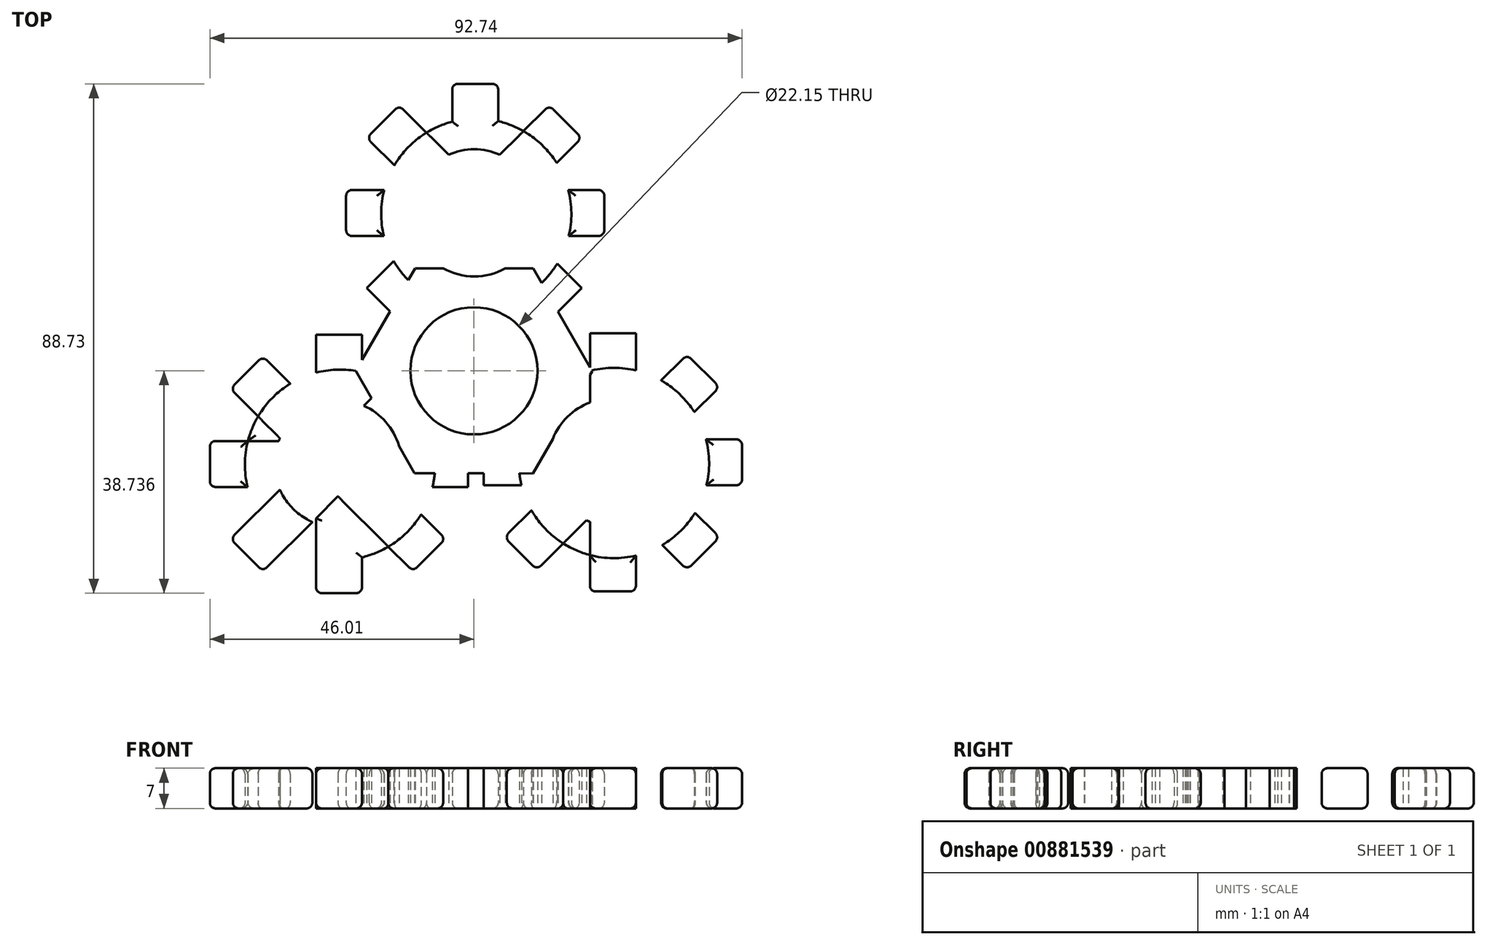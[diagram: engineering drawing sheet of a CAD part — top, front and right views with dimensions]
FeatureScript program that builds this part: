
annotation { "Feature Type Name" : "Feature", "Feature Type Description" : "" }
export const myFeature = defineFeature(function(context is Context, id is Id, definition is map)
    precondition{}
    {
        {
            var Q0;
            Q0=qCreatedBy(makeId("Top.planeOp"),FACE);
            var sketch = newSketch(context, id + "F0", { "sketchPlane" : qUnion([Q0])});
            skLineSegment(sketch, "E0.bottom", {"start": v(28.23, -45) * mm, "end": v(20.23, -45) * mm});
            skLineSegment(sketch, "E0.top", {"start": v(28.23, 0) * mm, "end": v(20.23, 0) * mm});
            skLineSegment(sketch, "E0.left", {"start": v(28.23, -45) * mm, "end": v(28.23, 0) * mm});
            skLineSegment(sketch, "E0.right", {"start": v(20.23, -45) * mm, "end": v(20.23, 0) * mm});
            skPoint(sketch, "E0.middle", {"position": v(24.23, -22.5) * mm});
            skLineSegment(sketch, "E1.bottom", {"start": v(46.73, -26.5) * mm, "end": v(1.73, -26.5) * mm});
            skLineSegment(sketch, "E1.top", {"start": v(46.73, -18.5) * mm, "end": v(1.73, -18.5) * mm});
            skLineSegment(sketch, "E1.left", {"start": v(46.73, -26.5) * mm, "end": v(46.73, -18.5) * mm});
            skLineSegment(sketch, "E1.right", {"start": v(1.73, -26.5) * mm, "end": v(1.73, -18.5) * mm});
            skPoint(sketch, "E2.middle", {"position": v(24.41, -22.64) * mm});
            skLineSegment(sketch, "E3.bottom", {"start": v(42.8, -35.57) * mm, "end": v(37.14, -41.22) * mm});
            skLineSegment(sketch, "E3.top", {"start": v(10.98, -3.75) * mm, "end": v(5.32, -9.4) * mm});
            skLineSegment(sketch, "E3.left", {"start": v(42.8, -35.57) * mm, "end": v(10.98, -3.75) * mm});
            skLineSegment(sketch, "E3.right", {"start": v(37.14, -41.22) * mm, "end": v(5.32, -9.4) * mm});
            skPoint(sketch, "E3.middle", {"position": v(24.06, -22.48) * mm});
            skLineSegment(sketch, "E4.bottom", {"start": v(42.8, -9.4) * mm, "end": v(10.98, -41.22) * mm});
            skLineSegment(sketch, "E4.top", {"start": v(37.14, -3.75) * mm, "end": v(5.32, -35.57) * mm});
            skLineSegment(sketch, "E4.left", {"start": v(42.8, -9.4) * mm, "end": v(37.14, -3.75) * mm});
            skLineSegment(sketch, "E4.right", {"start": v(10.98, -41.22) * mm, "end": v(5.32, -35.57) * mm});
            skPoint(sketch, "E5.middle", {"position": v(24.28, -22.44) * mm});
            skCircle(sketch, "E6", {"center": v(24.06, -22.48) * mm, "radius": 11.07 * mm});
            skCircle(sketch, "E7", {"center": v(24.41, -22.64) * mm, "radius": 16.57 * mm});
            skLineSegment(sketch, "E8.bottom", {"start": v(-19.51, -45.31) * mm, "end": v(-27.51, -45.31) * mm});
            skLineSegment(sketch, "E8.top", {"start": v(-19.51, -0.31) * mm, "end": v(-27.51, -0.31) * mm});
            skLineSegment(sketch, "E8.left", {"start": v(-19.51, -45.31) * mm, "end": v(-19.51, -0.31) * mm});
            skLineSegment(sketch, "E8.right", {"start": v(-27.51, -45.31) * mm, "end": v(-27.51, -0.31) * mm});
            skPoint(sketch, "E8.middle", {"position": v(-23.51, -22.81) * mm});
            skLineSegment(sketch, "E9.bottom", {"start": v(-1.01, -26.81) * mm, "end": v(-46.01, -26.81) * mm});
            skLineSegment(sketch, "E9.top", {"start": v(-1.01, -18.81) * mm, "end": v(-46.01, -18.81) * mm});
            skLineSegment(sketch, "E9.left", {"start": v(-1.01, -26.81) * mm, "end": v(-1.01, -18.81) * mm});
            skLineSegment(sketch, "E9.right", {"start": v(-46.01, -26.81) * mm, "end": v(-46.01, -18.81) * mm});
            skPoint(sketch, "E10.middle", {"position": v(-23.33, -22.94) * mm});
            skLineSegment(sketch, "E11.bottom", {"start": v(-4.95, -35.87) * mm, "end": v(-10.6, -41.52) * mm});
            skLineSegment(sketch, "E11.top", {"start": v(-36.77, -4.05) * mm, "end": v(-42.42, -9.7) * mm});
            skLineSegment(sketch, "E11.left", {"start": v(-4.95, -35.87) * mm, "end": v(-36.77, -4.05) * mm});
            skLineSegment(sketch, "E11.right", {"start": v(-10.6, -41.52) * mm, "end": v(-42.42, -9.7) * mm});
            skPoint(sketch, "E11.middle", {"position": v(-23.68, -22.79) * mm});
            skLineSegment(sketch, "E12.bottom", {"start": v(-4.95, -9.7) * mm, "end": v(-36.77, -41.52) * mm});
            skLineSegment(sketch, "E12.top", {"start": v(-10.6, -4.05) * mm, "end": v(-42.42, -35.87) * mm});
            skLineSegment(sketch, "E12.left", {"start": v(-4.95, -9.7) * mm, "end": v(-10.6, -4.05) * mm});
            skLineSegment(sketch, "E12.right", {"start": v(-36.77, -41.52) * mm, "end": v(-42.42, -35.87) * mm});
            skPoint(sketch, "E13.middle", {"position": v(-23.47, -22.75) * mm});
            skCircle(sketch, "E14", {"center": v(-23.68, -22.79) * mm, "radius": 11.07 * mm});
            skCircle(sketch, "E15", {"center": v(-23.33, -22.94) * mm, "radius": 16.57 * mm});
            skLineSegment(sketch, "E16.bottom", {"start": v(4.23, -1.58) * mm, "end": v(-3.77, -1.58) * mm});
            skLineSegment(sketch, "E16.top", {"start": v(4.23, 43.42) * mm, "end": v(-3.77, 43.42) * mm});
            skLineSegment(sketch, "E16.left", {"start": v(4.23, -1.58) * mm, "end": v(4.23, 43.42) * mm});
            skLineSegment(sketch, "E16.right", {"start": v(-3.77, -1.58) * mm, "end": v(-3.77, 43.42) * mm});
            skPoint(sketch, "E16.middle", {"position": v(0.23, 20.92) * mm});
            skLineSegment(sketch, "E17.bottom", {"start": v(22.73, 16.92) * mm, "end": v(-22.27, 16.92) * mm});
            skLineSegment(sketch, "E17.top", {"start": v(22.73, 24.92) * mm, "end": v(-22.27, 24.92) * mm});
            skLineSegment(sketch, "E17.left", {"start": v(22.73, 16.92) * mm, "end": v(22.73, 24.92) * mm});
            skLineSegment(sketch, "E17.right", {"start": v(-22.27, 16.92) * mm, "end": v(-22.27, 24.92) * mm});
            skPoint(sketch, "E18.middle", {"position": v(0.41, 20.8) * mm});
            skLineSegment(sketch, "E19.bottom", {"start": v(18.8, 7.86) * mm, "end": v(13.14, 2.2) * mm});
            skLineSegment(sketch, "E19.top", {"start": v(-13.02, 39.68) * mm, "end": v(-18.68, 34.03) * mm});
            skLineSegment(sketch, "E19.left", {"start": v(18.8, 7.86) * mm, "end": v(-13.02, 39.68) * mm});
            skLineSegment(sketch, "E19.right", {"start": v(13.14, 2.2) * mm, "end": v(-18.68, 34.03) * mm});
            skPoint(sketch, "E19.middle", {"position": v(0.06, 20.95) * mm});
            skLineSegment(sketch, "E20.bottom", {"start": v(18.8, 34.03) * mm, "end": v(-13.02, 2.2) * mm});
            skLineSegment(sketch, "E20.top", {"start": v(13.14, 39.68) * mm, "end": v(-18.68, 7.86) * mm});
            skLineSegment(sketch, "E20.left", {"start": v(18.8, 34.03) * mm, "end": v(13.14, 39.68) * mm});
            skLineSegment(sketch, "E20.right", {"start": v(-13.02, 2.2) * mm, "end": v(-18.68, 7.86) * mm});
            skPoint(sketch, "E21.middle", {"position": v(0.28, 20.98) * mm});
            skCircle(sketch, "E22", {"center": v(0.06, 20.95) * mm, "radius": 11.07 * mm});
            skCircle(sketch, "E23", {"center": v(0.41, 20.8) * mm, "radius": 16.57 * mm});
            skPoint(sketch, "E24.cCircle.centerSnap0", {"position": v(8.15, -6.57) * mm});
            skPoint(sketch, "E24.0.midPoint", {"position": v(15.43, -15.54) * mm});
            skCircle(sketch, "E25.cCircle", {"center": v(0, -6.57) * mm, "radius": 17.85 * mm, "construction": true});
            skLineSegment(sketch, "E25.0", {"start": v(20.6, -6.63) * mm, "end": v(10.26, -24.45) * mm});
            skLineSegment(sketch, "E25.1", {"start": v(10.26, -24.45) * mm, "end": v(-10.35, -24.4) * mm});
            skLineSegment(sketch, "E25.2", {"start": v(-10.35, -24.4) * mm, "end": v(-20.6, -6.52) * mm});
            skLineSegment(sketch, "E25.3", {"start": v(-20.6, -6.52) * mm, "end": v(-10.26, 11.3) * mm});
            skLineSegment(sketch, "E25.4", {"start": v(-10.26, 11.3) * mm, "end": v(10.35, 11.25) * mm});
            skLineSegment(sketch, "E25.5", {"start": v(10.35, 11.25) * mm, "end": v(20.6, -6.63) * mm});
            skCircle(sketch, "E26", {"center": v(0, -6.57) * mm, "radius": 11.07 * mm});
            skSolve(sketch);
        }
        {
            var Q0;
            {var subQ0=sQuery(id+"F0.wireOp",EDGE,"E19.top");Q0=makeQuery(id+"F0.imprint","IMPRINT",FACE,{"disambiguationData":[TD([[makeQuery(id+"F0.imprint","IMPRINT",EDGE,{"derivedFrom":subQ0}),1.0]])]});}
            var Q1;
            {var subQ0=sQuery(id+"F0.wireOp",EDGE,"E23");var subQ1=sQuery(id+"F0.wireOp",EDGE,"E19.left");var subQ2=makeQuery(id+"F0.imprint","INTERSECT",VERTEX,{"disambiguationData":[OD(1.0)],"derivedFrom":[subQ1,subQ0]});Q1=makeQuery(id+"F0.imprint","IMPRINT",FACE,{"disambiguationData":[TD([[makeQuery(id+"F0.imprint","IMPRINT",EDGE,{"disambiguationData":[TD([[subQ2,1.0]])],"derivedFrom":subQ1}),1.0]])]});}
            var Q2;
            {var subQ0=sQuery(id+"F0.wireOp",EDGE,"E23");var subQ1=sQuery(id+"F0.wireOp",EDGE,"E16.right");var subQ2=makeQuery(id+"F0.imprint","INTERSECT",VERTEX,{"disambiguationData":[OD(0.0)],"derivedFrom":[subQ1,subQ0]});Q2=makeQuery(id+"F0.imprint","IMPRINT",FACE,{"disambiguationData":[TD([[makeQuery(id+"F0.imprint","IMPRINT",EDGE,{"disambiguationData":[TD([[subQ2,1.0]])],"derivedFrom":subQ1}),1.0]])]});}
            var Q3;
            {var subQ0=sQuery(id+"F0.wireOp",EDGE,"E23");var subQ1=sQuery(id+"F0.wireOp",EDGE,"E16.left");var subQ2=makeQuery(id+"F0.imprint","INTERSECT",VERTEX,{"disambiguationData":[OD(0.0)],"derivedFrom":[subQ1,subQ0]});Q3=makeQuery(id+"F0.imprint","IMPRINT",FACE,{"disambiguationData":[TD([[makeQuery(id+"F0.imprint","IMPRINT",EDGE,{"disambiguationData":[TD([[subQ2,1.0]])],"derivedFrom":subQ1}),1.0]])]});}
            var Q4;
            {var subQ0=sQuery(id+"F0.wireOp",EDGE,"E16.top");Q4=makeQuery(id+"F0.imprint","IMPRINT",FACE,{"disambiguationData":[TD([[makeQuery(id+"F0.imprint","IMPRINT",EDGE,{"derivedFrom":subQ0}),1.0]])]});}
            var Q5;
            {var subQ0=sQuery(id+"F0.wireOp",EDGE,"E23");var subQ1=sQuery(id+"F0.wireOp",EDGE,"E16.left");var subQ2=makeQuery(id+"F0.imprint","INTERSECT",VERTEX,{"disambiguationData":[OD(0.0)],"derivedFrom":[subQ1,subQ0]});Q5=makeQuery(id+"F0.imprint","IMPRINT",FACE,{"disambiguationData":[TD([[makeQuery(id+"F0.imprint","IMPRINT",EDGE,{"disambiguationData":[TD([[subQ2,1.0]])],"derivedFrom":subQ1}),-1.0]])]});}
            var Q6;
            {var subQ0=sQuery(id+"F0.wireOp",EDGE,"E23");var subQ1=sQuery(id+"F0.wireOp",EDGE,"E20.bottom");var subQ2=makeQuery(id+"F0.imprint","INTERSECT",VERTEX,{"disambiguationData":[OD(0.0)],"derivedFrom":[subQ1,subQ0]});Q6=makeQuery(id+"F0.imprint","IMPRINT",FACE,{"disambiguationData":[TD([[makeQuery(id+"F0.imprint","IMPRINT",EDGE,{"disambiguationData":[TD([[subQ2,-1.0]])],"derivedFrom":subQ1}),-1.0]])]});}
            var Q7;
            {var subQ0=sQuery(id+"F0.wireOp",EDGE,"E20.left");Q7=makeQuery(id+"F0.imprint","IMPRINT",FACE,{"disambiguationData":[TD([[makeQuery(id+"F0.imprint","IMPRINT",EDGE,{"derivedFrom":subQ0}),1.0]])]});}
            var Q8;
            {var subQ0=sQuery(id+"F0.wireOp",EDGE,"E23");var subQ1=sQuery(id+"F0.wireOp",EDGE,"E17.top");var subQ2=makeQuery(id+"F0.imprint","INTERSECT",VERTEX,{"disambiguationData":[OD(0.0)],"derivedFrom":[subQ1,subQ0]});Q8=makeQuery(id+"F0.imprint","IMPRINT",FACE,{"disambiguationData":[TD([[makeQuery(id+"F0.imprint","IMPRINT",EDGE,{"disambiguationData":[TD([[subQ2,-1.0]])],"derivedFrom":subQ1}),-1.0]])]});}
            var Q9;
            {var subQ0=sQuery(id+"F0.wireOp",EDGE,"E23");var subQ1=sQuery(id+"F0.wireOp",EDGE,"E17.bottom");var subQ2=makeQuery(id+"F0.imprint","INTERSECT",VERTEX,{"disambiguationData":[OD(0.0)],"derivedFrom":[subQ1,subQ0]});Q9=makeQuery(id+"F0.imprint","IMPRINT",FACE,{"disambiguationData":[TD([[makeQuery(id+"F0.imprint","IMPRINT",EDGE,{"disambiguationData":[TD([[subQ2,-1.0]])],"derivedFrom":subQ1}),-1.0]])]});}
            var Q10;
            {var subQ0=sQuery(id+"F0.wireOp",EDGE,"E17.left");Q10=makeQuery(id+"F0.imprint","IMPRINT",FACE,{"disambiguationData":[TD([[makeQuery(id+"F0.imprint","IMPRINT",EDGE,{"derivedFrom":subQ0}),1.0]])]});}
            var Q11;
            {var subQ0=sQuery(id+"F0.wireOp",EDGE,"E23");var subQ1=sQuery(id+"F0.wireOp",EDGE,"E17.bottom");var subQ2=makeQuery(id+"F0.imprint","INTERSECT",VERTEX,{"disambiguationData":[OD(0.0)],"derivedFrom":[subQ1,subQ0]});Q11=makeQuery(id+"F0.imprint","IMPRINT",FACE,{"disambiguationData":[TD([[makeQuery(id+"F0.imprint","IMPRINT",EDGE,{"disambiguationData":[TD([[subQ2,-1.0]])],"derivedFrom":subQ1}),1.0]])]});}
            var Q12;
            {var subQ0=sQuery(id+"F0.wireOp",EDGE,"E23");var subQ1=sQuery(id+"F0.wireOp",EDGE,"E17.top");var subQ2=makeQuery(id+"F0.imprint","INTERSECT",VERTEX,{"disambiguationData":[OD(1.0)],"derivedFrom":[subQ1,subQ0]});Q12=makeQuery(id+"F0.imprint","IMPRINT",FACE,{"disambiguationData":[TD([[makeQuery(id+"F0.imprint","IMPRINT",EDGE,{"disambiguationData":[TD([[subQ2,1.0]])],"derivedFrom":subQ1}),-1.0]])]});}
            var Q13;
            {var subQ0=sQuery(id+"F0.wireOp",EDGE,"E23");var subQ1=sQuery(id+"F0.wireOp",EDGE,"E17.bottom");var subQ2=makeQuery(id+"F0.imprint","INTERSECT",VERTEX,{"disambiguationData":[OD(1.0)],"derivedFrom":[subQ1,subQ0]});Q13=makeQuery(id+"F0.imprint","IMPRINT",FACE,{"disambiguationData":[TD([[makeQuery(id+"F0.imprint","IMPRINT",EDGE,{"disambiguationData":[TD([[subQ2,1.0]])],"derivedFrom":subQ1}),-1.0]])]});}
            var Q14;
            {var subQ0=sQuery(id+"F0.wireOp",EDGE,"E17.right");Q14=makeQuery(id+"F0.imprint","IMPRINT",FACE,{"disambiguationData":[TD([[makeQuery(id+"F0.imprint","IMPRINT",EDGE,{"derivedFrom":subQ0}),-1.0]])]});}
            var Q15;
            {var subQ0=sQuery(id+"F0.wireOp",EDGE,"E23");var subQ1=sQuery(id+"F0.wireOp",EDGE,"E17.bottom");var subQ2=makeQuery(id+"F0.imprint","INTERSECT",VERTEX,{"disambiguationData":[OD(1.0)],"derivedFrom":[subQ1,subQ0]});Q15=makeQuery(id+"F0.imprint","IMPRINT",FACE,{"disambiguationData":[TD([[makeQuery(id+"F0.imprint","IMPRINT",EDGE,{"disambiguationData":[TD([[subQ2,1.0]])],"derivedFrom":subQ1}),1.0]])]});}
            var Q16;
            {var subQ3=sQuery(id+"F0.wireOp",EDGE,"E23");var subQ5=sQuery(id+"F0.wireOp",EDGE,"E20.top");var subQ6=makeQuery(id+"F0.imprint","INTERSECT",VERTEX,{"disambiguationData":[OD(1.0)],"derivedFrom":[subQ5,subQ3]});Q16=makeQuery(id+"F0.imprint","IMPRINT",FACE,{"disambiguationData":[TD([[makeQuery(id+"F0.imprint","IMPRINT",EDGE,{"disambiguationData":[TD([[subQ6,1.0]])],"derivedFrom":subQ5}),1.0]])]});}
            var Q17;
            {var subQ0=sQuery(id+"F0.wireOp",EDGE,"E20.right");var subQ1=sQuery(id+"F0.wireOp",EDGE,"E20.top");var subQ2=makeQuery(id+"F0.imprint","INTERSECT",VERTEX,{"derivedFrom":[subQ1,subQ0]});Q17=makeQuery(id+"F0.imprint","IMPRINT",FACE,{"disambiguationData":[TD([[makeQuery(id+"F0.imprint","IMPRINT",EDGE,{"disambiguationData":[TD([[subQ2,1.0]])],"derivedFrom":subQ1}),1.0]])]});}
            var Q18;
            {var subQ0=sQuery(id+"F0.wireOp",EDGE,"E20.right");var subQ1=sQuery(id+"F0.wireOp",EDGE,"E20.bottom");var subQ2=makeQuery(id+"F0.imprint","INTERSECT",VERTEX,{"derivedFrom":[subQ1,subQ0]});Q18=makeQuery(id+"F0.imprint","IMPRINT",FACE,{"disambiguationData":[TD([[makeQuery(id+"F0.imprint","IMPRINT",EDGE,{"disambiguationData":[TD([[subQ2,1.0]])],"derivedFrom":subQ1}),-1.0]])]});}
            var Q19;
            {var subQ1=sQuery(id+"F0.wireOp",EDGE,"E16.left");var subQ5=sQuery(id+"F0.wireOp",EDGE,"E23");var subQ9=makeQuery(id+"F0.imprint","INTERSECT",VERTEX,{"disambiguationData":[OD(1.0)],"derivedFrom":[subQ1,subQ5]});Q19=makeQuery(id+"F0.imprint","IMPRINT",FACE,{"disambiguationData":[TD([[makeQuery(id+"F0.imprint","IMPRINT",EDGE,{"disambiguationData":[TD([[subQ9,-1.0]])],"derivedFrom":subQ1}),1.0]])]});}
            var Q20;
            {var subQ0=sQuery(id+"F0.wireOp",EDGE,"E23");var subQ1=sQuery(id+"F0.wireOp",EDGE,"E16.left");var subQ2=makeQuery(id+"F0.imprint","INTERSECT",VERTEX,{"disambiguationData":[OD(1.0)],"derivedFrom":[subQ1,subQ0]});Q20=makeQuery(id+"F0.imprint","IMPRINT",FACE,{"disambiguationData":[TD([[makeQuery(id+"F0.imprint","IMPRINT",EDGE,{"disambiguationData":[TD([[subQ2,-1.0]])],"derivedFrom":subQ1}),-1.0]])]});}
            var Q21;
            {var subQ0=sQuery(id+"F0.wireOp",EDGE,"E23");var subQ1=sQuery(id+"F0.wireOp",EDGE,"E19.right");var subQ2=makeQuery(id+"F0.imprint","INTERSECT",VERTEX,{"disambiguationData":[OD(1.0)],"derivedFrom":[subQ1,subQ0]});Q21=makeQuery(id+"F0.imprint","IMPRINT",FACE,{"disambiguationData":[TD([[makeQuery(id+"F0.imprint","IMPRINT",EDGE,{"disambiguationData":[TD([[subQ2,-1.0]])],"derivedFrom":subQ1}),-1.0]])]});}
            var Q22;
            {var subQ5=sQuery(id+"F0.wireOp",EDGE,"E23");var subQ6=sQuery(id+"F0.wireOp",EDGE,"E19.left");var subQ7=makeQuery(id+"F0.imprint","INTERSECT",VERTEX,{"disambiguationData":[OD(0.0)],"derivedFrom":[subQ6,subQ5]});Q22=makeQuery(id+"F0.imprint","IMPRINT",FACE,{"disambiguationData":[TD([[makeQuery(id+"F0.imprint","IMPRINT",EDGE,{"disambiguationData":[TD([[subQ7,-1.0]])],"derivedFrom":subQ6}),1.0]])]});}
            var Q23;
            {var subQ0=sQuery(id+"F0.wireOp",EDGE,"E19.left");var subQ1=sQuery(id+"F0.wireOp",EDGE,"E19.bottom");var subQ2=makeQuery(id+"F0.imprint","INTERSECT",VERTEX,{"derivedFrom":[subQ1,subQ0]});Q23=makeQuery(id+"F0.imprint","IMPRINT",FACE,{"disambiguationData":[TD([[makeQuery(id+"F0.imprint","IMPRINT",EDGE,{"disambiguationData":[TD([[subQ2,-1.0]])],"derivedFrom":subQ1}),-1.0]])]});}
            var Q24;
            {var subQ0=sQuery(id+"F0.wireOp",EDGE,"E19.right");var subQ1=sQuery(id+"F0.wireOp",EDGE,"E19.bottom");var subQ2=makeQuery(id+"F0.imprint","INTERSECT",VERTEX,{"derivedFrom":[subQ1,subQ0]});Q24=makeQuery(id+"F0.imprint","IMPRINT",FACE,{"disambiguationData":[TD([[makeQuery(id+"F0.imprint","IMPRINT",EDGE,{"disambiguationData":[TD([[subQ2,1.0]])],"derivedFrom":subQ1}),-1.0]])]});}
            var Q25;
            {var subQ5=sQuery(id+"F0.wireOp",EDGE,"E20.bottom");var subQ7=sQuery(id+"F0.wireOp",EDGE,"E22");var subQ8=makeQuery(id+"F0.imprint","INTERSECT",VERTEX,{"disambiguationData":[OD(1.0)],"derivedFrom":[subQ5,subQ7]});Q25=makeQuery(id+"F0.imprint","IMPRINT",FACE,{"disambiguationData":[TD([[makeQuery(id+"F0.imprint","IMPRINT",EDGE,{"disambiguationData":[TD([[subQ8,-1.0]])],"derivedFrom":subQ5}),-1.0]])]});}
            var Q26;
            {var subQ0=sQuery(id+"F0.wireOp",EDGE,"E23");var subQ1=sQuery(id+"F0.wireOp",EDGE,"E16.right");var subQ2=makeQuery(id+"F0.imprint","INTERSECT",VERTEX,{"disambiguationData":[OD(1.0)],"derivedFrom":[subQ1,subQ0]});Q26=makeQuery(id+"F0.imprint","IMPRINT",FACE,{"disambiguationData":[TD([[makeQuery(id+"F0.imprint","IMPRINT",EDGE,{"disambiguationData":[TD([[subQ2,-1.0]])],"derivedFrom":subQ1}),1.0]])]});}
            var Q27;
            {var subQ9=sQuery(id+"F0.wireOp",EDGE,"E25.3");var subQ10=sQuery(id+"F0.wireOp",EDGE,"E8.left");var subQ11=makeQuery(id+"F0.imprint","INTERSECT",VERTEX,{"derivedFrom":[subQ10,subQ9]});Q27=makeQuery(id+"F0.imprint","IMPRINT",FACE,{"disambiguationData":[TD([[makeQuery(id+"F0.imprint","IMPRINT",EDGE,{"disambiguationData":[TD([[subQ11,1.0]])],"derivedFrom":subQ10}),-1.0]])]});}
            var Q28;
            {var subQ1=sQuery(id+"F0.wireOp",EDGE,"E0.right");var subQ9=sQuery(id+"F0.wireOp",EDGE,"E25.5");var subQ10=makeQuery(id+"F0.imprint","INTERSECT",VERTEX,{"derivedFrom":[subQ1,subQ9]});Q28=makeQuery(id+"F0.imprint","IMPRINT",FACE,{"disambiguationData":[TD([[makeQuery(id+"F0.imprint","IMPRINT",EDGE,{"disambiguationData":[TD([[subQ10,1.0]])],"derivedFrom":subQ1}),1.0]])]});}
            var Q29;
            {var subQ0=sQuery(id+"F0.wireOp",EDGE,"E3.left");var subQ1=sQuery(id+"F0.wireOp",EDGE,"E3.top");var subQ2=makeQuery(id+"F0.imprint","INTERSECT",VERTEX,{"derivedFrom":[subQ1,subQ0]});Q29=makeQuery(id+"F0.imprint","IMPRINT",FACE,{"disambiguationData":[TD([[makeQuery(id+"F0.imprint","IMPRINT",EDGE,{"disambiguationData":[TD([[subQ2,-1.0]])],"derivedFrom":subQ1}),1.0]])]});}
            var Q30;
            {var subQ0=sQuery(id+"F0.wireOp",EDGE,"E1.right");var subQ1=sQuery(id+"F0.wireOp",EDGE,"E1.top");var subQ2=makeQuery(id+"F0.imprint","INTERSECT",VERTEX,{"derivedFrom":[subQ1,subQ0]});Q30=makeQuery(id+"F0.imprint","IMPRINT",FACE,{"disambiguationData":[TD([[makeQuery(id+"F0.imprint","IMPRINT",EDGE,{"disambiguationData":[TD([[subQ2,1.0]])],"derivedFrom":subQ1}),1.0]])]});}
            var Q31;
            {var subQ1=sQuery(id+"F0.wireOp",EDGE,"E1.top");var subQ10=sQuery(id+"F0.wireOp",EDGE,"E1.right");var subQ11=makeQuery(id+"F0.imprint","INTERSECT",VERTEX,{"derivedFrom":[subQ1,subQ10]});Q31=makeQuery(id+"F0.imprint","IMPRINT",FACE,{"disambiguationData":[TD([[makeQuery(id+"F0.imprint","IMPRINT",EDGE,{"disambiguationData":[TD([[subQ11,1.0]])],"derivedFrom":subQ1}),-1.0]])]});}
            var Q32;
            {var subQ0=sQuery(id+"F0.wireOp",EDGE,"E9.left");var subQ1=sQuery(id+"F0.wireOp",EDGE,"E9.top");var subQ2=makeQuery(id+"F0.imprint","INTERSECT",VERTEX,{"derivedFrom":[subQ1,subQ0]});Q32=makeQuery(id+"F0.imprint","IMPRINT",FACE,{"disambiguationData":[TD([[makeQuery(id+"F0.imprint","IMPRINT",EDGE,{"disambiguationData":[TD([[subQ2,-1.0]])],"derivedFrom":subQ1}),1.0]])]});}
            var Q33;
            {var subQ0=sQuery(id+"F0.wireOp",EDGE,"E15");var subQ1=sQuery(id+"F0.wireOp",EDGE,"E9.top");var subQ2=makeQuery(id+"F0.imprint","INTERSECT",VERTEX,{"disambiguationData":[OD(1.0)],"derivedFrom":[subQ1,subQ0]});Q33=makeQuery(id+"F0.imprint","IMPRINT",FACE,{"disambiguationData":[TD([[makeQuery(id+"F0.imprint","IMPRINT",EDGE,{"disambiguationData":[TD([[subQ2,-1.0]])],"derivedFrom":subQ1}),1.0]])]});}
            var Q34;
            {var subQ0=sQuery(id+"F0.wireOp",EDGE,"E15");var subQ1=sQuery(id+"F0.wireOp",EDGE,"E9.top");var subQ2=makeQuery(id+"F0.imprint","INTERSECT",VERTEX,{"disambiguationData":[OD(1.0)],"derivedFrom":[subQ1,subQ0]});Q34=makeQuery(id+"F0.imprint","IMPRINT",FACE,{"disambiguationData":[TD([[makeQuery(id+"F0.imprint","IMPRINT",EDGE,{"disambiguationData":[TD([[subQ2,-1.0]])],"derivedFrom":subQ1}),-1.0]])]});}
            var Q35;
            {var subQ1=sQuery(id+"F0.wireOp",EDGE,"E12.bottom");var subQ5=sQuery(id+"F0.wireOp",EDGE,"E15");var subQ9=makeQuery(id+"F0.imprint","INTERSECT",VERTEX,{"disambiguationData":[OD(1.0)],"derivedFrom":[subQ1,subQ5]});Q35=makeQuery(id+"F0.imprint","IMPRINT",FACE,{"disambiguationData":[TD([[makeQuery(id+"F0.imprint","IMPRINT",EDGE,{"disambiguationData":[TD([[subQ9,-1.0]])],"derivedFrom":subQ1}),-1.0]])]});}
            var Q36;
            {var subQ0=sQuery(id+"F0.wireOp",EDGE,"E25.2");var subQ1=sQuery(id+"F0.wireOp",EDGE,"E8.left");var subQ2=makeQuery(id+"F0.imprint","INTERSECT",VERTEX,{"derivedFrom":[subQ1,subQ0]});Q36=makeQuery(id+"F0.imprint","IMPRINT",FACE,{"disambiguationData":[TD([[makeQuery(id+"F0.imprint","IMPRINT",EDGE,{"disambiguationData":[TD([[subQ2,-1.0]])],"derivedFrom":subQ1}),-1.0]])]});}
            var Q37;
            {var subQ0=sQuery(id+"F0.wireOp",EDGE,"E26");var subQ1=sQuery(id+"F0.wireOp",EDGE,"E12.bottom");var subQ2=makeQuery(id+"F0.imprint","INTERSECT",VERTEX,{"derivedFrom":[subQ1,subQ0]});Q37=makeQuery(id+"F0.imprint","IMPRINT",FACE,{"disambiguationData":[TD([[makeQuery(id+"F0.imprint","IMPRINT",EDGE,{"disambiguationData":[TD([[subQ2,-1.0]])],"derivedFrom":subQ1}),-1.0]])]});}
            var Q38;
            {var subQ1=sQuery(id+"F0.wireOp",EDGE,"E1.top");var subQ7=sQuery(id+"F0.wireOp",EDGE,"E25.0");var subQ9=makeQuery(id+"F0.imprint","INTERSECT",VERTEX,{"derivedFrom":[subQ1,subQ7]});Q38=makeQuery(id+"F0.imprint","IMPRINT",FACE,{"disambiguationData":[TD([[makeQuery(id+"F0.imprint","IMPRINT",EDGE,{"disambiguationData":[TD([[subQ9,-1.0]])],"derivedFrom":subQ1}),-1.0]])]});}
            var Q39;
            {var subQ0=sQuery(id+"F0.wireOp",EDGE,"E25.0");var subQ1=sQuery(id+"F0.wireOp",EDGE,"E1.top");var subQ2=makeQuery(id+"F0.imprint","INTERSECT",VERTEX,{"derivedFrom":[subQ1,subQ0]});Q39=makeQuery(id+"F0.imprint","IMPRINT",FACE,{"disambiguationData":[TD([[makeQuery(id+"F0.imprint","IMPRINT",EDGE,{"disambiguationData":[TD([[subQ2,-1.0]])],"derivedFrom":subQ1}),1.0]])]});}
            var Q40;
            {var subQ1=sQuery(id+"F0.wireOp",EDGE,"E3.left");var subQ7=sQuery(id+"F0.wireOp",EDGE,"E25.0");var subQ9=makeQuery(id+"F0.imprint","INTERSECT",VERTEX,{"derivedFrom":[subQ1,subQ7]});Q40=makeQuery(id+"F0.imprint","IMPRINT",FACE,{"disambiguationData":[TD([[makeQuery(id+"F0.imprint","IMPRINT",EDGE,{"disambiguationData":[TD([[subQ9,-1.0]])],"derivedFrom":subQ1}),1.0]])]});}
            var Q41;
            {var subQ0=sQuery(id+"F0.wireOp",EDGE,"E25.0");var subQ1=sQuery(id+"F0.wireOp",EDGE,"E0.right");var subQ2=makeQuery(id+"F0.imprint","INTERSECT",VERTEX,{"derivedFrom":[subQ1,subQ0]});Q41=makeQuery(id+"F0.imprint","IMPRINT",FACE,{"disambiguationData":[TD([[makeQuery(id+"F0.imprint","IMPRINT",EDGE,{"disambiguationData":[TD([[subQ2,-1.0]])],"derivedFrom":subQ1}),1.0]])]});}
            var Q42;
            {var subQ0=sQuery(id+"F0.wireOp",EDGE,"E26");var subQ1=sQuery(id+"F0.wireOp",EDGE,"E16.left");var subQ2=makeQuery(id+"F0.imprint","INTERSECT",VERTEX,{"derivedFrom":[subQ1,subQ0]});Q42=makeQuery(id+"F0.imprint","IMPRINT",FACE,{"disambiguationData":[TD([[makeQuery(id+"F0.imprint","IMPRINT",EDGE,{"disambiguationData":[TD([[subQ2,-1.0]])],"derivedFrom":subQ1}),1.0]])]});}
            var Q43;
            {var subQ0=sQuery(id+"F0.wireOp",EDGE,"E26");var subQ1=sQuery(id+"F0.wireOp",EDGE,"E16.right");var subQ2=makeQuery(id+"F0.imprint","INTERSECT",VERTEX,{"derivedFrom":[subQ1,subQ0]});Q43=makeQuery(id+"F0.imprint","IMPRINT",FACE,{"disambiguationData":[TD([[makeQuery(id+"F0.imprint","IMPRINT",EDGE,{"disambiguationData":[TD([[subQ2,-1.0]])],"derivedFrom":subQ1}),-1.0]])]});}
            var Q44;
            {var subQ6=sQuery(id+"F0.wireOp",EDGE,"E0.top");Q44=makeQuery(id+"F0.imprint","IMPRINT",FACE,{"disambiguationData":[TD([[makeQuery(id+"F0.imprint","IMPRINT",EDGE,{"derivedFrom":subQ6}),1.0]])]});}
            var Q45;
            {var subQ0=sQuery(id+"F0.wireOp",EDGE,"E7");var subQ1=sQuery(id+"F0.wireOp",EDGE,"E0.left");var subQ2=makeQuery(id+"F0.imprint","INTERSECT",VERTEX,{"disambiguationData":[OD(1.0)],"derivedFrom":[subQ1,subQ0]});Q45=makeQuery(id+"F0.imprint","IMPRINT",FACE,{"disambiguationData":[TD([[makeQuery(id+"F0.imprint","IMPRINT",EDGE,{"disambiguationData":[TD([[subQ2,1.0]])],"derivedFrom":subQ1}),1.0]])]});}
            var Q46;
            {var subQ0=sQuery(id+"F0.wireOp",EDGE,"E6");var subQ1=sQuery(id+"F0.wireOp",EDGE,"E0.right");var subQ2=makeQuery(id+"F0.imprint","INTERSECT",VERTEX,{"disambiguationData":[OD(1.0)],"derivedFrom":[subQ1,subQ0]});Q46=makeQuery(id+"F0.imprint","IMPRINT",FACE,{"disambiguationData":[TD([[makeQuery(id+"F0.imprint","IMPRINT",EDGE,{"disambiguationData":[TD([[subQ2,-1.0]])],"derivedFrom":subQ1}),1.0]])]});}
            var Q47;
            {var subQ0=sQuery(id+"F0.wireOp",EDGE,"E6");var subQ1=sQuery(id+"F0.wireOp",EDGE,"E3.left");var subQ2=makeQuery(id+"F0.imprint","INTERSECT",VERTEX,{"disambiguationData":[OD(1.0)],"derivedFrom":[subQ1,subQ0]});Q47=makeQuery(id+"F0.imprint","IMPRINT",FACE,{"disambiguationData":[TD([[makeQuery(id+"F0.imprint","IMPRINT",EDGE,{"disambiguationData":[TD([[subQ2,-1.0]])],"derivedFrom":subQ1}),1.0]])]});}
            var Q48;
            {var subQ0=sQuery(id+"F0.wireOp",EDGE,"E25.0");var subQ1=sQuery(id+"F0.wireOp",EDGE,"E0.right");var subQ2=makeQuery(id+"F0.imprint","INTERSECT",VERTEX,{"derivedFrom":[subQ1,subQ0]});Q48=makeQuery(id+"F0.imprint","IMPRINT",FACE,{"disambiguationData":[TD([[makeQuery(id+"F0.imprint","IMPRINT",EDGE,{"disambiguationData":[TD([[subQ2,-1.0]])],"derivedFrom":subQ1}),-1.0]])]});}
            var Q49;
            {var subQ0=sQuery(id+"F0.wireOp",EDGE,"E25.5");var subQ1=sQuery(id+"F0.wireOp",EDGE,"E0.right");var subQ2=makeQuery(id+"F0.imprint","INTERSECT",VERTEX,{"derivedFrom":[subQ1,subQ0]});Q49=makeQuery(id+"F0.imprint","IMPRINT",FACE,{"disambiguationData":[TD([[makeQuery(id+"F0.imprint","IMPRINT",EDGE,{"disambiguationData":[TD([[subQ2,1.0]])],"derivedFrom":subQ1}),-1.0]])]});}
            var Q50;
            {var subQ0=sQuery(id+"F0.wireOp",EDGE,"E7");var subQ1=sQuery(id+"F0.wireOp",EDGE,"E0.left");var subQ2=makeQuery(id+"F0.imprint","INTERSECT",VERTEX,{"disambiguationData":[OD(1.0)],"derivedFrom":[subQ1,subQ0]});Q50=makeQuery(id+"F0.imprint","IMPRINT",FACE,{"disambiguationData":[TD([[makeQuery(id+"F0.imprint","IMPRINT",EDGE,{"disambiguationData":[TD([[subQ2,1.0]])],"derivedFrom":subQ1}),-1.0]])]});}
            var Q51;
            {var subQ0=sQuery(id+"F0.wireOp",EDGE,"E7");var subQ1=sQuery(id+"F0.wireOp",EDGE,"E4.bottom");var subQ2=makeQuery(id+"F0.imprint","INTERSECT",VERTEX,{"disambiguationData":[OD(0.0)],"derivedFrom":[subQ1,subQ0]});Q51=makeQuery(id+"F0.imprint","IMPRINT",FACE,{"disambiguationData":[TD([[makeQuery(id+"F0.imprint","IMPRINT",EDGE,{"disambiguationData":[TD([[subQ2,-1.0]])],"derivedFrom":subQ1}),-1.0]])]});}
            var Q52;
            {var subQ0=sQuery(id+"F0.wireOp",EDGE,"E4.left");Q52=makeQuery(id+"F0.imprint","IMPRINT",FACE,{"disambiguationData":[TD([[makeQuery(id+"F0.imprint","IMPRINT",EDGE,{"derivedFrom":subQ0}),1.0]])]});}
            var Q53;
            {var subQ0=sQuery(id+"F0.wireOp",EDGE,"E7");var subQ1=sQuery(id+"F0.wireOp",EDGE,"E1.top");var subQ2=makeQuery(id+"F0.imprint","INTERSECT",VERTEX,{"disambiguationData":[OD(0.0)],"derivedFrom":[subQ1,subQ0]});Q53=makeQuery(id+"F0.imprint","IMPRINT",FACE,{"disambiguationData":[TD([[makeQuery(id+"F0.imprint","IMPRINT",EDGE,{"disambiguationData":[TD([[subQ2,-1.0]])],"derivedFrom":subQ1}),-1.0]])]});}
            var Q54;
            {var subQ0=sQuery(id+"F0.wireOp",EDGE,"E7");var subQ1=sQuery(id+"F0.wireOp",EDGE,"E1.bottom");var subQ2=makeQuery(id+"F0.imprint","INTERSECT",VERTEX,{"disambiguationData":[OD(0.0)],"derivedFrom":[subQ1,subQ0]});Q54=makeQuery(id+"F0.imprint","IMPRINT",FACE,{"disambiguationData":[TD([[makeQuery(id+"F0.imprint","IMPRINT",EDGE,{"disambiguationData":[TD([[subQ2,-1.0]])],"derivedFrom":subQ1}),-1.0]])]});}
            var Q55;
            {var subQ0=sQuery(id+"F0.wireOp",EDGE,"E1.left");Q55=makeQuery(id+"F0.imprint","IMPRINT",FACE,{"disambiguationData":[TD([[makeQuery(id+"F0.imprint","IMPRINT",EDGE,{"derivedFrom":subQ0}),1.0]])]});}
            var Q56;
            {var subQ1=sQuery(id+"F0.wireOp",EDGE,"E1.bottom");var subQ5=sQuery(id+"F0.wireOp",EDGE,"E7");var subQ6=makeQuery(id+"F0.imprint","INTERSECT",VERTEX,{"disambiguationData":[OD(1.0)],"derivedFrom":[subQ1,subQ5]});Q56=makeQuery(id+"F0.imprint","IMPRINT",FACE,{"disambiguationData":[TD([[makeQuery(id+"F0.imprint","IMPRINT",EDGE,{"disambiguationData":[TD([[subQ6,1.0]])],"derivedFrom":subQ1}),-1.0]])]});}
            var Q57;
            {var subQ0=sQuery(id+"F0.wireOp",EDGE,"E7");var subQ1=sQuery(id+"F0.wireOp",EDGE,"E1.bottom");var subQ2=makeQuery(id+"F0.imprint","INTERSECT",VERTEX,{"disambiguationData":[OD(1.0)],"derivedFrom":[subQ1,subQ0]});Q57=makeQuery(id+"F0.imprint","IMPRINT",FACE,{"disambiguationData":[TD([[makeQuery(id+"F0.imprint","IMPRINT",EDGE,{"disambiguationData":[TD([[subQ2,1.0]])],"derivedFrom":subQ1}),1.0]])]});}
            var Q58;
            {var subQ0=sQuery(id+"F0.wireOp",EDGE,"E1.right");var subQ1=sQuery(id+"F0.wireOp",EDGE,"E1.bottom");var subQ2=makeQuery(id+"F0.imprint","INTERSECT",VERTEX,{"derivedFrom":[subQ1,subQ0]});Q58=makeQuery(id+"F0.imprint","IMPRINT",FACE,{"disambiguationData":[TD([[makeQuery(id+"F0.imprint","IMPRINT",EDGE,{"disambiguationData":[TD([[subQ2,1.0]])],"derivedFrom":subQ1}),-1.0]])]});}
            var Q59;
            {var subQ0=sQuery(id+"F0.wireOp",EDGE,"E7");var subQ1=sQuery(id+"F0.wireOp",EDGE,"E4.bottom");var subQ2=makeQuery(id+"F0.imprint","INTERSECT",VERTEX,{"disambiguationData":[OD(1.0)],"derivedFrom":[subQ1,subQ0]});Q59=makeQuery(id+"F0.imprint","IMPRINT",FACE,{"disambiguationData":[TD([[makeQuery(id+"F0.imprint","IMPRINT",EDGE,{"disambiguationData":[TD([[subQ2,1.0]])],"derivedFrom":subQ1}),-1.0]])]});}
            var Q60;
            {var subQ0=sQuery(id+"F0.wireOp",EDGE,"E7");var subQ1=sQuery(id+"F0.wireOp",EDGE,"E0.left");var subQ2=makeQuery(id+"F0.imprint","INTERSECT",VERTEX,{"disambiguationData":[OD(0.0)],"derivedFrom":[subQ1,subQ0]});Q60=makeQuery(id+"F0.imprint","IMPRINT",FACE,{"disambiguationData":[TD([[makeQuery(id+"F0.imprint","IMPRINT",EDGE,{"disambiguationData":[TD([[subQ2,-1.0]])],"derivedFrom":subQ1}),1.0]])]});}
            var Q61;
            {var subQ0=sQuery(id+"F0.wireOp",EDGE,"E7");var subQ1=sQuery(id+"F0.wireOp",EDGE,"E0.right");var subQ2=makeQuery(id+"F0.imprint","INTERSECT",VERTEX,{"disambiguationData":[OD(0.0)],"derivedFrom":[subQ1,subQ0]});Q61=makeQuery(id+"F0.imprint","IMPRINT",FACE,{"disambiguationData":[TD([[makeQuery(id+"F0.imprint","IMPRINT",EDGE,{"disambiguationData":[TD([[subQ2,-1.0]])],"derivedFrom":subQ1}),1.0]])]});}
            var Q62;
            {var subQ0=sQuery(id+"F0.wireOp",EDGE,"E0.bottom");Q62=makeQuery(id+"F0.imprint","IMPRINT",FACE,{"disambiguationData":[TD([[makeQuery(id+"F0.imprint","IMPRINT",EDGE,{"derivedFrom":subQ0}),-1.0]])]});}
            var Q63;
            {var subQ0=sQuery(id+"F0.wireOp",EDGE,"E4.right");Q63=makeQuery(id+"F0.imprint","IMPRINT",FACE,{"disambiguationData":[TD([[makeQuery(id+"F0.imprint","IMPRINT",EDGE,{"derivedFrom":subQ0}),-1.0]])]});}
            var Q64;
            {var subQ0=sQuery(id+"F0.wireOp",EDGE,"E7");var subQ1=sQuery(id+"F0.wireOp",EDGE,"E0.left");var subQ2=makeQuery(id+"F0.imprint","INTERSECT",VERTEX,{"disambiguationData":[OD(0.0)],"derivedFrom":[subQ1,subQ0]});Q64=makeQuery(id+"F0.imprint","IMPRINT",FACE,{"disambiguationData":[TD([[makeQuery(id+"F0.imprint","IMPRINT",EDGE,{"disambiguationData":[TD([[subQ2,-1.0]])],"derivedFrom":subQ1}),-1.0]])]});}
            var Q65;
            {var subQ0=sQuery(id+"F0.wireOp",EDGE,"E7");var subQ1=sQuery(id+"F0.wireOp",EDGE,"E3.left");var subQ2=makeQuery(id+"F0.imprint","INTERSECT",VERTEX,{"disambiguationData":[OD(0.0)],"derivedFrom":[subQ1,subQ0]});Q65=makeQuery(id+"F0.imprint","IMPRINT",FACE,{"disambiguationData":[TD([[makeQuery(id+"F0.imprint","IMPRINT",EDGE,{"disambiguationData":[TD([[subQ2,-1.0]])],"derivedFrom":subQ1}),1.0]])]});}
            var Q66;
            {var subQ0=sQuery(id+"F0.wireOp",EDGE,"E7");var subQ1=sQuery(id+"F0.wireOp",EDGE,"E1.bottom");var subQ2=makeQuery(id+"F0.imprint","INTERSECT",VERTEX,{"disambiguationData":[OD(0.0)],"derivedFrom":[subQ1,subQ0]});Q66=makeQuery(id+"F0.imprint","IMPRINT",FACE,{"disambiguationData":[TD([[makeQuery(id+"F0.imprint","IMPRINT",EDGE,{"disambiguationData":[TD([[subQ2,-1.0]])],"derivedFrom":subQ1}),1.0]])]});}
            var Q67;
            {var subQ0=sQuery(id+"F0.wireOp",EDGE,"E3.bottom");Q67=makeQuery(id+"F0.imprint","IMPRINT",FACE,{"disambiguationData":[TD([[makeQuery(id+"F0.imprint","IMPRINT",EDGE,{"derivedFrom":subQ0}),-1.0]])]});}
            var Q68;
            {var subQ0=sQuery(id+"F0.wireOp",EDGE,"E25.3");var subQ1=sQuery(id+"F0.wireOp",EDGE,"E8.left");var subQ2=makeQuery(id+"F0.imprint","INTERSECT",VERTEX,{"derivedFrom":[subQ1,subQ0]});Q68=makeQuery(id+"F0.imprint","IMPRINT",FACE,{"disambiguationData":[TD([[makeQuery(id+"F0.imprint","IMPRINT",EDGE,{"disambiguationData":[TD([[subQ2,1.0]])],"derivedFrom":subQ1}),1.0]])]});}
            var Q69;
            {var subQ0=sQuery(id+"F0.wireOp",EDGE,"E25.2");var subQ1=sQuery(id+"F0.wireOp",EDGE,"E8.left");var subQ2=makeQuery(id+"F0.imprint","INTERSECT",VERTEX,{"derivedFrom":[subQ1,subQ0]});Q69=makeQuery(id+"F0.imprint","IMPRINT",FACE,{"disambiguationData":[TD([[makeQuery(id+"F0.imprint","IMPRINT",EDGE,{"disambiguationData":[TD([[subQ2,-1.0]])],"derivedFrom":subQ1}),1.0]])]});}
            var Q70;
            {var subQ0=sQuery(id+"F0.wireOp",EDGE,"E11.top");Q70=makeQuery(id+"F0.imprint","IMPRINT",FACE,{"disambiguationData":[TD([[makeQuery(id+"F0.imprint","IMPRINT",EDGE,{"derivedFrom":subQ0}),1.0]])]});}
            var Q71;
            {var subQ1=sQuery(id+"F0.wireOp",EDGE,"E8.top");Q71=makeQuery(id+"F0.imprint","IMPRINT",FACE,{"disambiguationData":[TD([[makeQuery(id+"F0.imprint","IMPRINT",EDGE,{"derivedFrom":subQ1}),1.0]])]});}
            var Q72;
            {var subQ0=sQuery(id+"F0.wireOp",EDGE,"E14");var subQ1=sQuery(id+"F0.wireOp",EDGE,"E8.left");var subQ2=makeQuery(id+"F0.imprint","INTERSECT",VERTEX,{"disambiguationData":[OD(1.0)],"derivedFrom":[subQ1,subQ0]});Q72=makeQuery(id+"F0.imprint","IMPRINT",FACE,{"disambiguationData":[TD([[makeQuery(id+"F0.imprint","IMPRINT",EDGE,{"disambiguationData":[TD([[subQ2,-1.0]])],"derivedFrom":subQ1}),1.0]])]});}
            var Q73;
            {var subQ0=sQuery(id+"F0.wireOp",EDGE,"E14");var subQ1=sQuery(id+"F0.wireOp",EDGE,"E8.left");var subQ2=makeQuery(id+"F0.imprint","INTERSECT",VERTEX,{"disambiguationData":[OD(1.0)],"derivedFrom":[subQ1,subQ0]});Q73=makeQuery(id+"F0.imprint","IMPRINT",FACE,{"disambiguationData":[TD([[makeQuery(id+"F0.imprint","IMPRINT",EDGE,{"disambiguationData":[TD([[subQ2,-1.0]])],"derivedFrom":subQ1}),-1.0]])]});}
            var Q74;
            {var subQ0=sQuery(id+"F0.wireOp",EDGE,"E25.2");var subQ1=sQuery(id+"F0.wireOp",EDGE,"E12.top");var subQ2=makeQuery(id+"F0.imprint","INTERSECT",VERTEX,{"derivedFrom":[subQ1,subQ0]});Q74=makeQuery(id+"F0.imprint","IMPRINT",FACE,{"disambiguationData":[TD([[makeQuery(id+"F0.imprint","IMPRINT",EDGE,{"disambiguationData":[TD([[subQ2,-1.0]])],"derivedFrom":subQ1}),1.0]])]});}
            var Q75;
            {var subQ0=sQuery(id+"F0.wireOp",EDGE,"E15");var subQ1=sQuery(id+"F0.wireOp",EDGE,"E8.right");var subQ2=makeQuery(id+"F0.imprint","INTERSECT",VERTEX,{"disambiguationData":[OD(1.0)],"derivedFrom":[subQ1,subQ0]});Q75=makeQuery(id+"F0.imprint","IMPRINT",FACE,{"disambiguationData":[TD([[makeQuery(id+"F0.imprint","IMPRINT",EDGE,{"disambiguationData":[TD([[subQ2,1.0]])],"derivedFrom":subQ1}),1.0]])]});}
            var Q76;
            {var subQ0=sQuery(id+"F0.wireOp",EDGE,"E15");var subQ1=sQuery(id+"F0.wireOp",EDGE,"E11.left");var subQ2=makeQuery(id+"F0.imprint","INTERSECT",VERTEX,{"disambiguationData":[OD(1.0)],"derivedFrom":[subQ1,subQ0]});Q76=makeQuery(id+"F0.imprint","IMPRINT",FACE,{"disambiguationData":[TD([[makeQuery(id+"F0.imprint","IMPRINT",EDGE,{"disambiguationData":[TD([[subQ2,1.0]])],"derivedFrom":subQ1}),1.0]])]});}
            var Q77;
            {var subQ0=sQuery(id+"F0.wireOp",EDGE,"E15");var subQ1=sQuery(id+"F0.wireOp",EDGE,"E9.top");var subQ2=makeQuery(id+"F0.imprint","INTERSECT",VERTEX,{"disambiguationData":[OD(0.0)],"derivedFrom":[subQ1,subQ0]});Q77=makeQuery(id+"F0.imprint","IMPRINT",FACE,{"disambiguationData":[TD([[makeQuery(id+"F0.imprint","IMPRINT",EDGE,{"disambiguationData":[TD([[subQ2,1.0]])],"derivedFrom":subQ1}),-1.0]])]});}
            var Q78;
            {var subQ0=sQuery(id+"F0.wireOp",EDGE,"E15");var subQ1=sQuery(id+"F0.wireOp",EDGE,"E9.bottom");var subQ2=makeQuery(id+"F0.imprint","INTERSECT",VERTEX,{"disambiguationData":[OD(1.0)],"derivedFrom":[subQ1,subQ0]});Q78=makeQuery(id+"F0.imprint","IMPRINT",FACE,{"disambiguationData":[TD([[makeQuery(id+"F0.imprint","IMPRINT",EDGE,{"disambiguationData":[TD([[subQ2,1.0]])],"derivedFrom":subQ1}),-1.0]])]});}
            var Q79;
            {var subQ0=sQuery(id+"F0.wireOp",EDGE,"E9.right");Q79=makeQuery(id+"F0.imprint","IMPRINT",FACE,{"disambiguationData":[TD([[makeQuery(id+"F0.imprint","IMPRINT",EDGE,{"derivedFrom":subQ0}),-1.0]])]});}
            var Q80;
            {var subQ0=sQuery(id+"F0.wireOp",EDGE,"E15");var subQ1=sQuery(id+"F0.wireOp",EDGE,"E9.bottom");var subQ2=makeQuery(id+"F0.imprint","INTERSECT",VERTEX,{"disambiguationData":[OD(1.0)],"derivedFrom":[subQ1,subQ0]});Q80=makeQuery(id+"F0.imprint","IMPRINT",FACE,{"disambiguationData":[TD([[makeQuery(id+"F0.imprint","IMPRINT",EDGE,{"disambiguationData":[TD([[subQ2,1.0]])],"derivedFrom":subQ1}),1.0]])]});}
            var Q81;
            {var subQ0=sQuery(id+"F0.wireOp",EDGE,"E15");var subQ1=sQuery(id+"F0.wireOp",EDGE,"E12.bottom");var subQ2=makeQuery(id+"F0.imprint","INTERSECT",VERTEX,{"disambiguationData":[OD(0.0)],"derivedFrom":[subQ1,subQ0]});Q81=makeQuery(id+"F0.imprint","IMPRINT",FACE,{"disambiguationData":[TD([[makeQuery(id+"F0.imprint","IMPRINT",EDGE,{"disambiguationData":[TD([[subQ2,1.0]])],"derivedFrom":subQ1}),-1.0]])]});}
            var Q82;
            {var subQ0=sQuery(id+"F0.wireOp",EDGE,"E12.right");Q82=makeQuery(id+"F0.imprint","IMPRINT",FACE,{"disambiguationData":[TD([[makeQuery(id+"F0.imprint","IMPRINT",EDGE,{"derivedFrom":subQ0}),-1.0]])]});}
            var Q83;
            {var subQ0=sQuery(id+"F0.wireOp",EDGE,"E15");var subQ1=sQuery(id+"F0.wireOp",EDGE,"E8.right");var subQ2=makeQuery(id+"F0.imprint","INTERSECT",VERTEX,{"disambiguationData":[OD(0.0)],"derivedFrom":[subQ1,subQ0]});Q83=makeQuery(id+"F0.imprint","IMPRINT",FACE,{"disambiguationData":[TD([[makeQuery(id+"F0.imprint","IMPRINT",EDGE,{"disambiguationData":[TD([[subQ2,-1.0]])],"derivedFrom":subQ1}),1.0]])]});}
            var Q84;
            {var subQ0=sQuery(id+"F0.wireOp",EDGE,"E15");var subQ1=sQuery(id+"F0.wireOp",EDGE,"E8.left");var subQ2=makeQuery(id+"F0.imprint","INTERSECT",VERTEX,{"disambiguationData":[OD(0.0)],"derivedFrom":[subQ1,subQ0]});Q84=makeQuery(id+"F0.imprint","IMPRINT",FACE,{"disambiguationData":[TD([[makeQuery(id+"F0.imprint","IMPRINT",EDGE,{"disambiguationData":[TD([[subQ2,-1.0]])],"derivedFrom":subQ1}),1.0]])]});}
            var Q85;
            {var subQ0=sQuery(id+"F0.wireOp",EDGE,"E8.bottom");Q85=makeQuery(id+"F0.imprint","IMPRINT",FACE,{"disambiguationData":[TD([[makeQuery(id+"F0.imprint","IMPRINT",EDGE,{"derivedFrom":subQ0}),-1.0]])]});}
            var Q86;
            {var subQ0=sQuery(id+"F0.wireOp",EDGE,"E15");var subQ1=sQuery(id+"F0.wireOp",EDGE,"E8.left");var subQ2=makeQuery(id+"F0.imprint","INTERSECT",VERTEX,{"disambiguationData":[OD(0.0)],"derivedFrom":[subQ1,subQ0]});Q86=makeQuery(id+"F0.imprint","IMPRINT",FACE,{"disambiguationData":[TD([[makeQuery(id+"F0.imprint","IMPRINT",EDGE,{"disambiguationData":[TD([[subQ2,-1.0]])],"derivedFrom":subQ1}),-1.0]])]});}
            var Q87;
            {var subQ0=sQuery(id+"F0.wireOp",EDGE,"E15");var subQ1=sQuery(id+"F0.wireOp",EDGE,"E11.left");var subQ2=makeQuery(id+"F0.imprint","INTERSECT",VERTEX,{"disambiguationData":[OD(0.0)],"derivedFrom":[subQ1,subQ0]});Q87=makeQuery(id+"F0.imprint","IMPRINT",FACE,{"disambiguationData":[TD([[makeQuery(id+"F0.imprint","IMPRINT",EDGE,{"disambiguationData":[TD([[subQ2,-1.0]])],"derivedFrom":subQ1}),1.0]])]});}
            var Q88;
            {var subQ0=sQuery(id+"F0.wireOp",EDGE,"E11.bottom");Q88=makeQuery(id+"F0.imprint","IMPRINT",FACE,{"disambiguationData":[TD([[makeQuery(id+"F0.imprint","IMPRINT",EDGE,{"derivedFrom":subQ0}),-1.0]])]});}
            var Q89;
            {var subQ3=sQuery(id+"F0.wireOp",EDGE,"E15");var subQ5=sQuery(id+"F0.wireOp",EDGE,"E9.bottom");var subQ6=makeQuery(id+"F0.imprint","INTERSECT",VERTEX,{"disambiguationData":[OD(0.0)],"derivedFrom":[subQ5,subQ3]});Q89=makeQuery(id+"F0.imprint","IMPRINT",FACE,{"disambiguationData":[TD([[makeQuery(id+"F0.imprint","IMPRINT",EDGE,{"disambiguationData":[TD([[subQ6,-1.0]])],"derivedFrom":subQ5}),-1.0]])]});}
            var Q90;
            {var subQ0=sQuery(id+"F0.wireOp",EDGE,"E9.left");var subQ1=sQuery(id+"F0.wireOp",EDGE,"E9.bottom");var subQ2=makeQuery(id+"F0.imprint","INTERSECT",VERTEX,{"derivedFrom":[subQ1,subQ0]});Q90=makeQuery(id+"F0.imprint","IMPRINT",FACE,{"disambiguationData":[TD([[makeQuery(id+"F0.imprint","IMPRINT",EDGE,{"disambiguationData":[TD([[subQ2,-1.0]])],"derivedFrom":subQ1}),-1.0]])]});}
            var Q91;
            {var subQ0=sQuery(id+"F0.wireOp",EDGE,"E15");var subQ1=sQuery(id+"F0.wireOp",EDGE,"E9.bottom");var subQ2=makeQuery(id+"F0.imprint","INTERSECT",VERTEX,{"disambiguationData":[OD(0.0)],"derivedFrom":[subQ1,subQ0]});Q91=makeQuery(id+"F0.imprint","IMPRINT",FACE,{"disambiguationData":[TD([[makeQuery(id+"F0.imprint","IMPRINT",EDGE,{"disambiguationData":[TD([[subQ2,-1.0]])],"derivedFrom":subQ1}),1.0]])]});}
            extrude(context, id + "F1", {"entities" : qUnion([Q0, Q1, Q2, Q3, Q4, Q5, Q6, Q7, Q8, Q9, Q10, Q11, Q12, Q13, Q14, Q15, Q16, Q17, Q18, Q19, Q20, Q21, Q22, Q23, Q24, Q25, Q26, Q27, Q28, Q29, Q30, Q31, Q32, Q33, Q34, Q35, Q36, Q37, Q38, Q39, Q40, Q41, Q42, Q43, Q44, Q45, Q46, Q47, Q48, Q49, Q50, Q51, Q52, Q53, Q54, Q55, Q56, Q57, Q58, Q59, Q60, Q61, Q62, Q63, Q64, Q65, Q66, Q67, Q68, Q69, Q70, Q71, Q72, Q73, Q74, Q75, Q76, Q77, Q78, Q79, Q80, Q81, Q82, Q83, Q84, Q85, Q86, Q87, Q88, Q89, Q90, Q91]), "depth" : 7 * mm, "offsetDistance" : 25 * mm});
        }
        {
            var Q0;
            Q0=makeQuery(id+"F1.opExtrude","CAP_EDGE",EDGE,{"disambiguationData":[OSD([sQuery(id+"F0.wireOp",EDGE,"E16.top")])],"isStart":false});
            var Q1;
            Q1=makeQuery(id+"F1.opExtrude","CAP_EDGE",EDGE,{"disambiguationData":[OSD([sQuery(id+"F0.wireOp",EDGE,"E16.left")])],"isStart":false});
            var Q2;
            Q2=makeQuery(id+"F1.opExtrude","CAP_EDGE",EDGE,{"disambiguationData":[OSD([sQuery(id+"F0.wireOp",EDGE,"E16.right")])],"isStart":false});
            var Q3;
            {var subQ0=sQuery(id+"F0.wireOp",EDGE,"E23");Q3=makeQuery(id+"F1.opExtrude","CAP_EDGE",EDGE,{"disambiguationData":[OSD([subQ0]),TDD([makeQuery(id+"F0.imprint","IMPRINT",EDGE,{"disambiguationData":[TD([[makeQuery(id+"F0.imprint","INTERSECT",VERTEX,{"disambiguationData":[OD(0.0)],"derivedFrom":[sQuery(id+"F0.wireOp",EDGE,"E16.left"),subQ0]}),1.0]])],"derivedFrom":subQ0})])],"isStart":false});}
            var Q4;
            {var subQ0=sQuery(id+"F0.wireOp",EDGE,"E20.top");Q4=makeQuery(id+"F1.opExtrude","CAP_EDGE",EDGE,{"disambiguationData":[OSD([subQ0]),TDD([makeQuery(id+"F0.imprint","IMPRINT",EDGE,{"disambiguationData":[TD([[makeQuery(id+"F0.imprint","INTERSECT",VERTEX,{"derivedFrom":[subQ0,sQuery(id+"F0.wireOp",EDGE,"E20.left")]}),-1.0]])],"derivedFrom":subQ0})])],"isStart":false});}
            var Q5;
            Q5=makeQuery(id+"F1.opExtrude","CAP_EDGE",EDGE,{"disambiguationData":[OSD([sQuery(id+"F0.wireOp",EDGE,"E20.left")])],"isStart":false});
            var Q6;
            Q6=makeQuery(id+"F1.opExtrude","CAP_EDGE",EDGE,{"disambiguationData":[OSD([sQuery(id+"F0.wireOp",EDGE,"E20.bottom")])],"isStart":false});
            var Q7;
            {var subQ0=sQuery(id+"F0.wireOp",EDGE,"E23");Q7=makeQuery(id+"F1.opExtrude","CAP_EDGE",EDGE,{"disambiguationData":[OSD([subQ0]),TDD([makeQuery(id+"F0.imprint","IMPRINT",EDGE,{"disambiguationData":[TD([[makeQuery(id+"F0.imprint","INTERSECT",VERTEX,{"disambiguationData":[OD(0.0)],"derivedFrom":[sQuery(id+"F0.wireOp",EDGE,"E17.top"),subQ0]}),-1.0]])],"derivedFrom":subQ0})])],"isStart":false});}
            var Q8;
            {var subQ0=sQuery(id+"F0.wireOp",EDGE,"E17.top");Q8=makeQuery(id+"F1.opExtrude","CAP_EDGE",EDGE,{"disambiguationData":[OSD([subQ0]),TDD([makeQuery(id+"F0.imprint","IMPRINT",EDGE,{"disambiguationData":[TD([[makeQuery(id+"F0.imprint","INTERSECT",VERTEX,{"derivedFrom":[subQ0,sQuery(id+"F0.wireOp",EDGE,"E17.left")]}),-1.0]])],"derivedFrom":subQ0})])],"isStart":false});}
            var Q9;
            Q9=makeQuery(id+"F1.opExtrude","CAP_EDGE",EDGE,{"disambiguationData":[OSD([sQuery(id+"F0.wireOp",EDGE,"E17.left")])],"isStart":false});
            var Q10;
            {var subQ0=sQuery(id+"F0.wireOp",EDGE,"E17.bottom");Q10=makeQuery(id+"F1.opExtrude","CAP_EDGE",EDGE,{"disambiguationData":[OSD([subQ0]),TDD([makeQuery(id+"F0.imprint","IMPRINT",EDGE,{"disambiguationData":[TD([[makeQuery(id+"F0.imprint","INTERSECT",VERTEX,{"derivedFrom":[subQ0,sQuery(id+"F0.wireOp",EDGE,"E17.left")]}),-1.0]])],"derivedFrom":subQ0})])],"isStart":false});}
            var Q11;
            {var subQ0=sQuery(id+"F0.wireOp",EDGE,"E23");Q11=makeQuery(id+"F1.opExtrude","CAP_EDGE",EDGE,{"disambiguationData":[OSD([subQ0]),TDD([makeQuery(id+"F0.imprint","IMPRINT",EDGE,{"disambiguationData":[TD([[makeQuery(id+"F0.imprint","INTERSECT",VERTEX,{"disambiguationData":[OD(0.0)],"derivedFrom":[sQuery(id+"F0.wireOp",EDGE,"E17.bottom"),subQ0]}),1.0]])],"derivedFrom":subQ0})])],"isStart":false});}
            var Q12;
            {var subQ0=sQuery(id+"F0.wireOp",EDGE,"E19.left");Q12=makeQuery(id+"F1.opExtrude","CAP_EDGE",EDGE,{"disambiguationData":[OSD([subQ0]),TDD([makeQuery(id+"F0.imprint","IMPRINT",EDGE,{"disambiguationData":[TD([[makeQuery(id+"F0.imprint","INTERSECT",VERTEX,{"derivedFrom":[sQuery(id+"F0.wireOp",EDGE,"E19.bottom"),subQ0]}),-1.0]])],"derivedFrom":subQ0})])],"isStart":false});}
            var Q13;
            {var subQ0=sQuery(id+"F0.wireOp",EDGE,"E19.left");Q13=makeQuery(id+"F1.opExtrude","CAP_EDGE",EDGE,{"disambiguationData":[OSD([subQ0]),TDD([makeQuery(id+"F0.imprint","IMPRINT",EDGE,{"disambiguationData":[TD([[makeQuery(id+"F0.imprint","INTERSECT",VERTEX,{"derivedFrom":[sQuery(id+"F0.wireOp",EDGE,"E19.top"),subQ0]}),1.0]])],"derivedFrom":subQ0})])],"isStart":false});}
            var Q14;
            {var subQ0=sQuery(id+"F0.wireOp",EDGE,"E23");Q14=makeQuery(id+"F1.opExtrude","CAP_EDGE",EDGE,{"disambiguationData":[OSD([subQ0]),TDD([makeQuery(id+"F0.imprint","IMPRINT",EDGE,{"disambiguationData":[TD([[makeQuery(id+"F0.imprint","INTERSECT",VERTEX,{"disambiguationData":[OD(0.0)],"derivedFrom":[sQuery(id+"F0.wireOp",EDGE,"E16.right"),subQ0]}),-1.0]])],"derivedFrom":subQ0})])],"isStart":false});}
            var Q15;
            Q15=makeQuery(id+"F1.opExtrude","CAP_EDGE",EDGE,{"disambiguationData":[OSD([sQuery(id+"F0.wireOp",EDGE,"E19.top")])],"isStart":false});
            var Q16;
            Q16=makeQuery(id+"F1.opExtrude","CAP_EDGE",EDGE,{"disambiguationData":[OSD([sQuery(id+"F0.wireOp",EDGE,"E19.right")])],"isStart":false});
            var Q17;
            {var subQ0=sQuery(id+"F0.wireOp",EDGE,"E23");Q17=makeQuery(id+"F1.opExtrude","CAP_EDGE",EDGE,{"disambiguationData":[OSD([subQ0]),TDD([makeQuery(id+"F0.imprint","IMPRINT",EDGE,{"disambiguationData":[TD([[makeQuery(id+"F0.imprint","INTERSECT",VERTEX,{"disambiguationData":[OD(1.0)],"derivedFrom":[sQuery(id+"F0.wireOp",EDGE,"E17.top"),subQ0]}),1.0]])],"derivedFrom":subQ0})])],"isStart":false});}
            var Q18;
            {var subQ0=sQuery(id+"F0.wireOp",EDGE,"E17.top");Q18=makeQuery(id+"F1.opExtrude","CAP_EDGE",EDGE,{"disambiguationData":[OSD([subQ0]),TDD([makeQuery(id+"F0.imprint","IMPRINT",EDGE,{"disambiguationData":[TD([[makeQuery(id+"F0.imprint","INTERSECT",VERTEX,{"derivedFrom":[subQ0,sQuery(id+"F0.wireOp",EDGE,"E17.right")]}),1.0]])],"derivedFrom":subQ0})])],"isStart":false});}
            var Q19;
            Q19=makeQuery(id+"F1.opExtrude","CAP_EDGE",EDGE,{"disambiguationData":[OSD([sQuery(id+"F0.wireOp",EDGE,"E17.right")])],"isStart":false});
            var Q20;
            {var subQ0=sQuery(id+"F0.wireOp",EDGE,"E17.bottom");Q20=makeQuery(id+"F1.opExtrude","CAP_EDGE",EDGE,{"disambiguationData":[OSD([subQ0]),TDD([makeQuery(id+"F0.imprint","IMPRINT",EDGE,{"disambiguationData":[TD([[makeQuery(id+"F0.imprint","INTERSECT",VERTEX,{"derivedFrom":[subQ0,sQuery(id+"F0.wireOp",EDGE,"E17.right")]}),1.0]])],"derivedFrom":subQ0})])],"isStart":false});}
            var Q21;
            {var subQ0=sQuery(id+"F0.wireOp",EDGE,"E23");Q21=makeQuery(id+"F1.opExtrude","CAP_EDGE",EDGE,{"disambiguationData":[OSD([subQ0]),TDD([makeQuery(id+"F0.imprint","IMPRINT",EDGE,{"disambiguationData":[TD([[makeQuery(id+"F0.imprint","INTERSECT",VERTEX,{"disambiguationData":[OD(1.0)],"derivedFrom":[sQuery(id+"F0.wireOp",EDGE,"E17.bottom"),subQ0]}),-1.0]])],"derivedFrom":subQ0})])],"isStart":false});}
            var Q22;
            {var subQ0=sQuery(id+"F0.wireOp",EDGE,"E20.top");Q22=makeQuery(id+"F1.opExtrude","CAP_EDGE",EDGE,{"disambiguationData":[OSD([subQ0]),TDD([makeQuery(id+"F0.imprint","IMPRINT",EDGE,{"disambiguationData":[TD([[makeQuery(id+"F0.imprint","INTERSECT",VERTEX,{"derivedFrom":[subQ0,sQuery(id+"F0.wireOp",EDGE,"E20.right")]}),1.0]])],"derivedFrom":subQ0})])],"isStart":false});}
            var Q23;
            Q23=makeQuery(id+"F1.opExtrude","CAP_EDGE",EDGE,{"disambiguationData":[OSD([sQuery(id+"F0.wireOp",EDGE,"E20.right")])],"isStart":false});
            var Q24;
            Q24=makeQuery(id+"F1.opExtrude","CAP_EDGE",EDGE,{"disambiguationData":[OSD([sQuery(id+"F0.wireOp",EDGE,"E19.bottom")])],"isStart":false});
            var Q25;
            Q25=makeQuery(id+"F1.opExtrude","CAP_EDGE",EDGE,{"disambiguationData":[OSD([sQuery(id+"F0.wireOp",EDGE,"E25.5")])],"isStart":false});
            var Q26;
            Q26=makeQuery(id+"F1.opExtrude","CAP_EDGE",EDGE,{"disambiguationData":[OSD([sQuery(id+"F0.wireOp",EDGE,"E25.3")])],"isStart":false});
            var Q27;
            {var subQ0=sQuery(id+"F0.wireOp",EDGE,"E0.right");Q27=makeQuery(id+"F1.opExtrude","CAP_EDGE",EDGE,{"disambiguationData":[OSD([subQ0]),TDD([makeQuery(id+"F0.imprint","IMPRINT",EDGE,{"disambiguationData":[TD([[makeQuery(id+"F0.imprint","INTERSECT",VERTEX,{"derivedFrom":[sQuery(id+"F0.wireOp",EDGE,"E0.top"),subQ0]}),1.0]])],"derivedFrom":subQ0})])],"isStart":false});}
            var Q28;
            Q28=makeQuery(id+"F1.opExtrude","CAP_EDGE",EDGE,{"disambiguationData":[OSD([sQuery(id+"F0.wireOp",EDGE,"E0.top")])],"isStart":false});
            var Q29;
            {var subQ0=sQuery(id+"F0.wireOp",EDGE,"E0.left");Q29=makeQuery(id+"F1.opExtrude","CAP_EDGE",EDGE,{"disambiguationData":[OSD([subQ0]),TDD([makeQuery(id+"F0.imprint","IMPRINT",EDGE,{"disambiguationData":[TD([[makeQuery(id+"F0.imprint","INTERSECT",VERTEX,{"derivedFrom":[sQuery(id+"F0.wireOp",EDGE,"E0.top"),subQ0]}),1.0]])],"derivedFrom":subQ0})])],"isStart":false});}
            var Q30;
            {var subQ0=sQuery(id+"F0.wireOp",EDGE,"E7");Q30=makeQuery(id+"F1.opExtrude","CAP_EDGE",EDGE,{"disambiguationData":[OSD([subQ0]),TDD([makeQuery(id+"F0.imprint","IMPRINT",EDGE,{"disambiguationData":[TD([[makeQuery(id+"F0.imprint","INTERSECT",VERTEX,{"disambiguationData":[OD(1.0)],"derivedFrom":[sQuery(id+"F0.wireOp",EDGE,"E0.left"),subQ0]}),1.0]])],"derivedFrom":subQ0})])],"isStart":false});}
            var Q31;
            {var subQ0=sQuery(id+"F0.wireOp",EDGE,"E4.top");Q31=makeQuery(id+"F1.opExtrude","CAP_EDGE",EDGE,{"disambiguationData":[OSD([subQ0]),TDD([makeQuery(id+"F0.imprint","IMPRINT",EDGE,{"disambiguationData":[TD([[makeQuery(id+"F0.imprint","INTERSECT",VERTEX,{"derivedFrom":[subQ0,sQuery(id+"F0.wireOp",EDGE,"E4.left")]}),-1.0]])],"derivedFrom":subQ0})])],"isStart":false});}
            var Q32;
            Q32=makeQuery(id+"F1.opExtrude","CAP_EDGE",EDGE,{"disambiguationData":[OSD([sQuery(id+"F0.wireOp",EDGE,"E4.left")])],"isStart":false});
            var Q33;
            {var subQ0=sQuery(id+"F0.wireOp",EDGE,"E4.bottom");Q33=makeQuery(id+"F1.opExtrude","CAP_EDGE",EDGE,{"disambiguationData":[OSD([subQ0]),TDD([makeQuery(id+"F0.imprint","IMPRINT",EDGE,{"disambiguationData":[TD([[makeQuery(id+"F0.imprint","INTERSECT",VERTEX,{"derivedFrom":[subQ0,sQuery(id+"F0.wireOp",EDGE,"E4.left")]}),-1.0]])],"derivedFrom":subQ0})])],"isStart":false});}
            var Q34;
            {var subQ0=sQuery(id+"F0.wireOp",EDGE,"E7");Q34=makeQuery(id+"F1.opExtrude","CAP_EDGE",EDGE,{"disambiguationData":[OSD([subQ0]),TDD([makeQuery(id+"F0.imprint","IMPRINT",EDGE,{"disambiguationData":[TD([[makeQuery(id+"F0.imprint","INTERSECT",VERTEX,{"disambiguationData":[OD(0.0)],"derivedFrom":[sQuery(id+"F0.wireOp",EDGE,"E1.top"),subQ0]}),-1.0]])],"derivedFrom":subQ0})])],"isStart":false});}
            var Q35;
            {var subQ0=sQuery(id+"F0.wireOp",EDGE,"E1.top");Q35=makeQuery(id+"F1.opExtrude","CAP_EDGE",EDGE,{"disambiguationData":[OSD([subQ0]),TDD([makeQuery(id+"F0.imprint","IMPRINT",EDGE,{"disambiguationData":[TD([[makeQuery(id+"F0.imprint","INTERSECT",VERTEX,{"derivedFrom":[subQ0,sQuery(id+"F0.wireOp",EDGE,"E1.left")]}),-1.0]])],"derivedFrom":subQ0})])],"isStart":false});}
            var Q36;
            Q36=makeQuery(id+"F1.opExtrude","CAP_EDGE",EDGE,{"disambiguationData":[OSD([sQuery(id+"F0.wireOp",EDGE,"E1.left")])],"isStart":false});
            var Q37;
            {var subQ0=sQuery(id+"F0.wireOp",EDGE,"E1.bottom");Q37=makeQuery(id+"F1.opExtrude","CAP_EDGE",EDGE,{"disambiguationData":[OSD([subQ0]),TDD([makeQuery(id+"F0.imprint","IMPRINT",EDGE,{"disambiguationData":[TD([[makeQuery(id+"F0.imprint","INTERSECT",VERTEX,{"derivedFrom":[subQ0,sQuery(id+"F0.wireOp",EDGE,"E1.left")]}),-1.0]])],"derivedFrom":subQ0})])],"isStart":false});}
            var Q38;
            {var subQ0=sQuery(id+"F0.wireOp",EDGE,"E7");Q38=makeQuery(id+"F1.opExtrude","CAP_EDGE",EDGE,{"disambiguationData":[OSD([subQ0]),TDD([makeQuery(id+"F0.imprint","IMPRINT",EDGE,{"disambiguationData":[TD([[makeQuery(id+"F0.imprint","INTERSECT",VERTEX,{"disambiguationData":[OD(0.0)],"derivedFrom":[sQuery(id+"F0.wireOp",EDGE,"E1.bottom"),subQ0]}),1.0]])],"derivedFrom":subQ0})])],"isStart":false});}
            var Q39;
            Q39=makeQuery(id+"F1.opExtrude","CAP_EDGE",EDGE,{"disambiguationData":[OSD([sQuery(id+"F0.wireOp",EDGE,"E3.left")])],"isStart":false});
            var Q40;
            Q40=makeQuery(id+"F1.opExtrude","CAP_EDGE",EDGE,{"disambiguationData":[OSD([sQuery(id+"F0.wireOp",EDGE,"E3.right")])],"isStart":false});
            var Q41;
            Q41=makeQuery(id+"F1.opExtrude","CAP_EDGE",EDGE,{"disambiguationData":[OSD([sQuery(id+"F0.wireOp",EDGE,"E3.bottom")])],"isStart":false});
            var Q42;
            {var subQ0=sQuery(id+"F0.wireOp",EDGE,"E7");Q42=makeQuery(id+"F1.opExtrude","CAP_EDGE",EDGE,{"disambiguationData":[OSD([subQ0]),TDD([makeQuery(id+"F0.imprint","IMPRINT",EDGE,{"disambiguationData":[TD([[makeQuery(id+"F0.imprint","INTERSECT",VERTEX,{"disambiguationData":[OD(0.0)],"derivedFrom":[sQuery(id+"F0.wireOp",EDGE,"E0.left"),subQ0]}),-1.0]])],"derivedFrom":subQ0})])],"isStart":false});}
            var Q43;
            {var subQ0=sQuery(id+"F0.wireOp",EDGE,"E0.left");Q43=makeQuery(id+"F1.opExtrude","CAP_EDGE",EDGE,{"disambiguationData":[OSD([subQ0]),TDD([makeQuery(id+"F0.imprint","IMPRINT",EDGE,{"disambiguationData":[TD([[makeQuery(id+"F0.imprint","INTERSECT",VERTEX,{"derivedFrom":[sQuery(id+"F0.wireOp",EDGE,"E0.bottom"),subQ0]}),-1.0]])],"derivedFrom":subQ0})])],"isStart":false});}
            var Q44;
            Q44=makeQuery(id+"F1.opExtrude","CAP_EDGE",EDGE,{"disambiguationData":[OSD([sQuery(id+"F0.wireOp",EDGE,"E0.bottom")])],"isStart":false});
            var Q45;
            {var subQ0=sQuery(id+"F0.wireOp",EDGE,"E0.right");Q45=makeQuery(id+"F1.opExtrude","CAP_EDGE",EDGE,{"disambiguationData":[OSD([subQ0]),TDD([makeQuery(id+"F0.imprint","IMPRINT",EDGE,{"disambiguationData":[TD([[makeQuery(id+"F0.imprint","INTERSECT",VERTEX,{"derivedFrom":[sQuery(id+"F0.wireOp",EDGE,"E0.bottom"),subQ0]}),-1.0]])],"derivedFrom":subQ0})])],"isStart":false});}
            var Q46;
            {var subQ0=sQuery(id+"F0.wireOp",EDGE,"E7");Q46=makeQuery(id+"F1.opExtrude","CAP_EDGE",EDGE,{"disambiguationData":[OSD([subQ0]),TDD([makeQuery(id+"F0.imprint","IMPRINT",EDGE,{"disambiguationData":[TD([[makeQuery(id+"F0.imprint","INTERSECT",VERTEX,{"disambiguationData":[OD(0.0)],"derivedFrom":[sQuery(id+"F0.wireOp",EDGE,"E0.right"),subQ0]}),1.0]])],"derivedFrom":subQ0})])],"isStart":false});}
            var Q47;
            {var subQ0=sQuery(id+"F0.wireOp",EDGE,"E4.bottom");Q47=makeQuery(id+"F1.opExtrude","CAP_EDGE",EDGE,{"disambiguationData":[OSD([subQ0]),TDD([makeQuery(id+"F0.imprint","IMPRINT",EDGE,{"disambiguationData":[TD([[makeQuery(id+"F0.imprint","INTERSECT",VERTEX,{"derivedFrom":[subQ0,sQuery(id+"F0.wireOp",EDGE,"E4.right")]}),1.0]])],"derivedFrom":subQ0})])],"isStart":false});}
            var Q48;
            Q48=makeQuery(id+"F1.opExtrude","CAP_EDGE",EDGE,{"disambiguationData":[OSD([sQuery(id+"F0.wireOp",EDGE,"E4.right")])],"isStart":false});
            var Q49;
            {var subQ0=sQuery(id+"F0.wireOp",EDGE,"E4.top");Q49=makeQuery(id+"F1.opExtrude","CAP_EDGE",EDGE,{"disambiguationData":[OSD([subQ0]),TDD([makeQuery(id+"F0.imprint","IMPRINT",EDGE,{"disambiguationData":[TD([[makeQuery(id+"F0.imprint","INTERSECT",VERTEX,{"derivedFrom":[subQ0,sQuery(id+"F0.wireOp",EDGE,"E4.right")]}),1.0]])],"derivedFrom":subQ0})])],"isStart":false});}
            var Q50;
            {var subQ0=sQuery(id+"F0.wireOp",EDGE,"E7");Q50=makeQuery(id+"F1.opExtrude","CAP_EDGE",EDGE,{"disambiguationData":[OSD([subQ0]),TDD([makeQuery(id+"F0.imprint","IMPRINT",EDGE,{"disambiguationData":[TD([[makeQuery(id+"F0.imprint","INTERSECT",VERTEX,{"disambiguationData":[OD(1.0)],"derivedFrom":[sQuery(id+"F0.wireOp",EDGE,"E1.bottom"),subQ0]}),-1.0]])],"derivedFrom":subQ0})])],"isStart":false});}
            var Q51;
            {var subQ0=sQuery(id+"F0.wireOp",EDGE,"E1.bottom");Q51=makeQuery(id+"F1.opExtrude","CAP_EDGE",EDGE,{"disambiguationData":[OSD([subQ0]),TDD([makeQuery(id+"F0.imprint","IMPRINT",EDGE,{"disambiguationData":[TD([[makeQuery(id+"F0.imprint","INTERSECT",VERTEX,{"derivedFrom":[subQ0,sQuery(id+"F0.wireOp",EDGE,"E1.right")]}),1.0]])],"derivedFrom":subQ0})])],"isStart":false});}
            var Q52;
            Q52=makeQuery(id+"F1.opExtrude","CAP_EDGE",EDGE,{"disambiguationData":[OSD([sQuery(id+"F0.wireOp",EDGE,"E25.1")])],"isStart":false});
            var Q53;
            Q53=makeQuery(id+"F1.opExtrude","CAP_EDGE",EDGE,{"disambiguationData":[OSD([sQuery(id+"F0.wireOp",EDGE,"E1.right")])],"isStart":false});
            var Q54;
            Q54=makeQuery(id+"F1.opExtrude","CAP_EDGE",EDGE,{"disambiguationData":[OSD([sQuery(id+"F0.wireOp",EDGE,"E9.left")])],"isStart":false});
            var Q55;
            {var subQ0=sQuery(id+"F0.wireOp",EDGE,"E9.bottom");Q55=makeQuery(id+"F1.opExtrude","CAP_EDGE",EDGE,{"disambiguationData":[OSD([subQ0]),TDD([makeQuery(id+"F0.imprint","IMPRINT",EDGE,{"disambiguationData":[TD([[makeQuery(id+"F0.imprint","INTERSECT",VERTEX,{"derivedFrom":[subQ0,sQuery(id+"F0.wireOp",EDGE,"E9.left")]}),-1.0]])],"derivedFrom":subQ0})])],"isStart":false});}
            var Q56;
            {var subQ0=sQuery(id+"F0.wireOp",EDGE,"E15");Q56=makeQuery(id+"F1.opExtrude","CAP_EDGE",EDGE,{"disambiguationData":[OSD([subQ0]),TDD([makeQuery(id+"F0.imprint","IMPRINT",EDGE,{"disambiguationData":[TD([[makeQuery(id+"F0.imprint","INTERSECT",VERTEX,{"disambiguationData":[OD(0.0)],"derivedFrom":[sQuery(id+"F0.wireOp",EDGE,"E9.bottom"),subQ0]}),1.0]])],"derivedFrom":subQ0})])],"isStart":false});}
            var Q57;
            {var subQ0=sQuery(id+"F0.wireOp",EDGE,"E11.left");Q57=makeQuery(id+"F1.opExtrude","CAP_EDGE",EDGE,{"disambiguationData":[OSD([subQ0]),TDD([makeQuery(id+"F0.imprint","IMPRINT",EDGE,{"disambiguationData":[TD([[makeQuery(id+"F0.imprint","INTERSECT",VERTEX,{"derivedFrom":[sQuery(id+"F0.wireOp",EDGE,"E11.bottom"),subQ0]}),-1.0]])],"derivedFrom":subQ0})])],"isStart":false});}
            var Q58;
            {var subQ0=sQuery(id+"F0.wireOp",EDGE,"E11.right");Q58=makeQuery(id+"F1.opExtrude","CAP_EDGE",EDGE,{"disambiguationData":[OSD([subQ0]),TDD([makeQuery(id+"F0.imprint","IMPRINT",EDGE,{"disambiguationData":[TD([[makeQuery(id+"F0.imprint","INTERSECT",VERTEX,{"derivedFrom":[sQuery(id+"F0.wireOp",EDGE,"E11.bottom"),subQ0]}),-1.0]])],"derivedFrom":subQ0})])],"isStart":false});}
            var Q59;
            Q59=makeQuery(id+"F1.opExtrude","CAP_EDGE",EDGE,{"disambiguationData":[OSD([sQuery(id+"F0.wireOp",EDGE,"E11.bottom")])],"isStart":false});
            var Q60;
            {var subQ0=sQuery(id+"F0.wireOp",EDGE,"E15");Q60=makeQuery(id+"F1.opExtrude","CAP_EDGE",EDGE,{"disambiguationData":[OSD([subQ0]),TDD([makeQuery(id+"F0.imprint","IMPRINT",EDGE,{"disambiguationData":[TD([[makeQuery(id+"F0.imprint","INTERSECT",VERTEX,{"disambiguationData":[OD(0.0)],"derivedFrom":[sQuery(id+"F0.wireOp",EDGE,"E8.left"),subQ0]}),-1.0]])],"derivedFrom":subQ0})])],"isStart":false});}
            var Q61;
            Q61=makeQuery(id+"F1.opExtrude","CAP_EDGE",EDGE,{"disambiguationData":[OSD([sQuery(id+"F0.wireOp",EDGE,"E8.top")])],"isStart":false});
            var Q62;
            {var subQ0=sQuery(id+"F0.wireOp",EDGE,"E8.left");Q62=makeQuery(id+"F1.opExtrude","CAP_EDGE",EDGE,{"disambiguationData":[OSD([subQ0]),TDD([makeQuery(id+"F0.imprint","IMPRINT",EDGE,{"disambiguationData":[TD([[makeQuery(id+"F0.imprint","INTERSECT",VERTEX,{"derivedFrom":[sQuery(id+"F0.wireOp",EDGE,"E8.top"),subQ0]}),1.0]])],"derivedFrom":subQ0})])],"isStart":false});}
            var Q63;
            {var subQ0=sQuery(id+"F0.wireOp",EDGE,"E8.right");Q63=makeQuery(id+"F1.opExtrude","CAP_EDGE",EDGE,{"disambiguationData":[OSD([subQ0]),TDD([makeQuery(id+"F0.imprint","IMPRINT",EDGE,{"disambiguationData":[TD([[makeQuery(id+"F0.imprint","INTERSECT",VERTEX,{"derivedFrom":[sQuery(id+"F0.wireOp",EDGE,"E8.top"),subQ0]}),1.0]])],"derivedFrom":subQ0})])],"isStart":false});}
            var Q64;
            {var subQ0=sQuery(id+"F0.wireOp",EDGE,"E15");Q64=makeQuery(id+"F1.opExtrude","CAP_EDGE",EDGE,{"disambiguationData":[OSD([subQ0]),TDD([makeQuery(id+"F0.imprint","IMPRINT",EDGE,{"disambiguationData":[TD([[makeQuery(id+"F0.imprint","INTERSECT",VERTEX,{"disambiguationData":[OD(1.0)],"derivedFrom":[sQuery(id+"F0.wireOp",EDGE,"E8.right"),subQ0]}),-1.0]])],"derivedFrom":subQ0})])],"isStart":false});}
            var Q65;
            {var subQ0=sQuery(id+"F0.wireOp",EDGE,"E11.left");Q65=makeQuery(id+"F1.opExtrude","CAP_EDGE",EDGE,{"disambiguationData":[OSD([subQ0]),TDD([makeQuery(id+"F0.imprint","IMPRINT",EDGE,{"disambiguationData":[TD([[makeQuery(id+"F0.imprint","INTERSECT",VERTEX,{"derivedFrom":[sQuery(id+"F0.wireOp",EDGE,"E11.top"),subQ0]}),1.0]])],"derivedFrom":subQ0})])],"isStart":false});}
            var Q66;
            Q66=makeQuery(id+"F1.opExtrude","CAP_EDGE",EDGE,{"disambiguationData":[OSD([sQuery(id+"F0.wireOp",EDGE,"E11.top")])],"isStart":false});
            var Q67;
            {var subQ0=sQuery(id+"F0.wireOp",EDGE,"E11.right");Q67=makeQuery(id+"F1.opExtrude","CAP_EDGE",EDGE,{"disambiguationData":[OSD([subQ0]),TDD([makeQuery(id+"F0.imprint","IMPRINT",EDGE,{"disambiguationData":[TD([[makeQuery(id+"F0.imprint","INTERSECT",VERTEX,{"derivedFrom":[sQuery(id+"F0.wireOp",EDGE,"E11.top"),subQ0]}),1.0]])],"derivedFrom":subQ0})])],"isStart":false});}
            var Q68;
            {var subQ0=sQuery(id+"F0.wireOp",EDGE,"E15");Q68=makeQuery(id+"F1.opExtrude","CAP_EDGE",EDGE,{"disambiguationData":[OSD([subQ0]),TDD([makeQuery(id+"F0.imprint","IMPRINT",EDGE,{"disambiguationData":[TD([[makeQuery(id+"F0.imprint","INTERSECT",VERTEX,{"disambiguationData":[OD(0.0)],"derivedFrom":[sQuery(id+"F0.wireOp",EDGE,"E9.top"),subQ0]}),1.0]])],"derivedFrom":subQ0})])],"isStart":false});}
            var Q69;
            Q69=makeQuery(id+"F1.opExtrude","CAP_EDGE",EDGE,{"disambiguationData":[OSD([sQuery(id+"F0.wireOp",EDGE,"E9.top")])],"isStart":false});
            var Q70;
            Q70=makeQuery(id+"F1.opExtrude","CAP_EDGE",EDGE,{"disambiguationData":[OSD([sQuery(id+"F0.wireOp",EDGE,"E9.right")])],"isStart":false});
            var Q71;
            {var subQ0=sQuery(id+"F0.wireOp",EDGE,"E9.bottom");Q71=makeQuery(id+"F1.opExtrude","CAP_EDGE",EDGE,{"disambiguationData":[OSD([subQ0]),TDD([makeQuery(id+"F0.imprint","IMPRINT",EDGE,{"disambiguationData":[TD([[makeQuery(id+"F0.imprint","INTERSECT",VERTEX,{"derivedFrom":[subQ0,sQuery(id+"F0.wireOp",EDGE,"E9.right")]}),1.0]])],"derivedFrom":subQ0})])],"isStart":false});}
            var Q72;
            {var subQ0=sQuery(id+"F0.wireOp",EDGE,"E15");Q72=makeQuery(id+"F1.opExtrude","CAP_EDGE",EDGE,{"disambiguationData":[OSD([subQ0]),TDD([makeQuery(id+"F0.imprint","IMPRINT",EDGE,{"disambiguationData":[TD([[makeQuery(id+"F0.imprint","INTERSECT",VERTEX,{"disambiguationData":[OD(1.0)],"derivedFrom":[sQuery(id+"F0.wireOp",EDGE,"E9.bottom"),subQ0]}),-1.0]])],"derivedFrom":subQ0})])],"isStart":false});}
            var Q73;
            Q73=makeQuery(id+"F1.opExtrude","CAP_EDGE",EDGE,{"disambiguationData":[OSD([sQuery(id+"F0.wireOp",EDGE,"E12.top")])],"isStart":false});
            var Q74;
            Q74=makeQuery(id+"F1.opExtrude","CAP_EDGE",EDGE,{"disambiguationData":[OSD([sQuery(id+"F0.wireOp",EDGE,"E12.right")])],"isStart":false});
            var Q75;
            Q75=makeQuery(id+"F1.opExtrude","CAP_EDGE",EDGE,{"disambiguationData":[OSD([sQuery(id+"F0.wireOp",EDGE,"E12.bottom")])],"isStart":false});
            var Q76;
            {var subQ0=sQuery(id+"F0.wireOp",EDGE,"E15");Q76=makeQuery(id+"F1.opExtrude","CAP_EDGE",EDGE,{"disambiguationData":[OSD([subQ0]),TDD([makeQuery(id+"F0.imprint","IMPRINT",EDGE,{"disambiguationData":[TD([[makeQuery(id+"F0.imprint","INTERSECT",VERTEX,{"disambiguationData":[OD(0.0)],"derivedFrom":[sQuery(id+"F0.wireOp",EDGE,"E8.right"),subQ0]}),1.0]])],"derivedFrom":subQ0})])],"isStart":false});}
            var Q77;
            {var subQ0=sQuery(id+"F0.wireOp",EDGE,"E8.right");Q77=makeQuery(id+"F1.opExtrude","CAP_EDGE",EDGE,{"disambiguationData":[OSD([subQ0]),TDD([makeQuery(id+"F0.imprint","IMPRINT",EDGE,{"disambiguationData":[TD([[makeQuery(id+"F0.imprint","INTERSECT",VERTEX,{"derivedFrom":[sQuery(id+"F0.wireOp",EDGE,"E8.bottom"),subQ0]}),-1.0]])],"derivedFrom":subQ0})])],"isStart":false});}
            var Q78;
            {var subQ0=sQuery(id+"F0.wireOp",EDGE,"E8.left");Q78=makeQuery(id+"F1.opExtrude","CAP_EDGE",EDGE,{"disambiguationData":[OSD([subQ0]),TDD([makeQuery(id+"F0.imprint","IMPRINT",EDGE,{"disambiguationData":[TD([[makeQuery(id+"F0.imprint","INTERSECT",VERTEX,{"derivedFrom":[sQuery(id+"F0.wireOp",EDGE,"E8.bottom"),subQ0]}),-1.0]])],"derivedFrom":subQ0})])],"isStart":false});}
            var Q79;
            Q79=makeQuery(id+"F1.opExtrude","CAP_EDGE",EDGE,{"disambiguationData":[OSD([sQuery(id+"F0.wireOp",EDGE,"E8.bottom")])],"isStart":false});
            var Q80;
            Q80=makeQuery(id+"F1.opExtrude","CAP_EDGE",EDGE,{"disambiguationData":[OSD([sQuery(id+"F0.wireOp",EDGE,"E8.bottom")])],"isStart":true});
            var Q81;
            {var subQ0=sQuery(id+"F0.wireOp",EDGE,"E8.left");Q81=makeQuery(id+"F1.opExtrude","CAP_EDGE",EDGE,{"disambiguationData":[OSD([subQ0]),TDD([makeQuery(id+"F0.imprint","IMPRINT",EDGE,{"disambiguationData":[TD([[makeQuery(id+"F0.imprint","INTERSECT",VERTEX,{"derivedFrom":[sQuery(id+"F0.wireOp",EDGE,"E8.bottom"),subQ0]}),-1.0]])],"derivedFrom":subQ0})])],"isStart":true});}
            var Q82;
            {var subQ0=sQuery(id+"F0.wireOp",EDGE,"E8.right");Q82=makeQuery(id+"F1.opExtrude","CAP_EDGE",EDGE,{"disambiguationData":[OSD([subQ0]),TDD([makeQuery(id+"F0.imprint","IMPRINT",EDGE,{"disambiguationData":[TD([[makeQuery(id+"F0.imprint","INTERSECT",VERTEX,{"derivedFrom":[sQuery(id+"F0.wireOp",EDGE,"E8.bottom"),subQ0]}),-1.0]])],"derivedFrom":subQ0})])],"isStart":true});}
            var Q83;
            {var subQ0=sQuery(id+"F0.wireOp",EDGE,"E15");Q83=makeQuery(id+"F1.opExtrude","CAP_EDGE",EDGE,{"disambiguationData":[OSD([subQ0]),TDD([makeQuery(id+"F0.imprint","IMPRINT",EDGE,{"disambiguationData":[TD([[makeQuery(id+"F0.imprint","INTERSECT",VERTEX,{"disambiguationData":[OD(0.0)],"derivedFrom":[sQuery(id+"F0.wireOp",EDGE,"E8.left"),subQ0]}),-1.0]])],"derivedFrom":subQ0})])],"isStart":true});}
            var Q84;
            {var subQ0=sQuery(id+"F0.wireOp",EDGE,"E11.right");Q84=makeQuery(id+"F1.opExtrude","CAP_EDGE",EDGE,{"disambiguationData":[OSD([subQ0]),TDD([makeQuery(id+"F0.imprint","IMPRINT",EDGE,{"disambiguationData":[TD([[makeQuery(id+"F0.imprint","INTERSECT",VERTEX,{"derivedFrom":[sQuery(id+"F0.wireOp",EDGE,"E11.bottom"),subQ0]}),-1.0]])],"derivedFrom":subQ0})])],"isStart":true});}
            var Q85;
            {var subQ0=sQuery(id+"F0.wireOp",EDGE,"E11.left");Q85=makeQuery(id+"F1.opExtrude","CAP_EDGE",EDGE,{"disambiguationData":[OSD([subQ0]),TDD([makeQuery(id+"F0.imprint","IMPRINT",EDGE,{"disambiguationData":[TD([[makeQuery(id+"F0.imprint","INTERSECT",VERTEX,{"derivedFrom":[sQuery(id+"F0.wireOp",EDGE,"E11.bottom"),subQ0]}),-1.0]])],"derivedFrom":subQ0})])],"isStart":true});}
            var Q86;
            Q86=makeQuery(id+"F1.opExtrude","CAP_EDGE",EDGE,{"disambiguationData":[OSD([sQuery(id+"F0.wireOp",EDGE,"E11.bottom")])],"isStart":true});
            var Q87;
            {var subQ0=sQuery(id+"F0.wireOp",EDGE,"E15");Q87=makeQuery(id+"F1.opExtrude","CAP_EDGE",EDGE,{"disambiguationData":[OSD([subQ0]),TDD([makeQuery(id+"F0.imprint","IMPRINT",EDGE,{"disambiguationData":[TD([[makeQuery(id+"F0.imprint","INTERSECT",VERTEX,{"disambiguationData":[OD(0.0)],"derivedFrom":[sQuery(id+"F0.wireOp",EDGE,"E9.bottom"),subQ0]}),1.0]])],"derivedFrom":subQ0})])],"isStart":true});}
            var Q88;
            {var subQ0=sQuery(id+"F0.wireOp",EDGE,"E9.bottom");Q88=makeQuery(id+"F1.opExtrude","CAP_EDGE",EDGE,{"disambiguationData":[OSD([subQ0]),TDD([makeQuery(id+"F0.imprint","IMPRINT",EDGE,{"disambiguationData":[TD([[makeQuery(id+"F0.imprint","INTERSECT",VERTEX,{"derivedFrom":[subQ0,sQuery(id+"F0.wireOp",EDGE,"E9.left")]}),-1.0]])],"derivedFrom":subQ0})])],"isStart":true});}
            var Q89;
            Q89=makeQuery(id+"F1.opExtrude","CAP_EDGE",EDGE,{"disambiguationData":[OSD([sQuery(id+"F0.wireOp",EDGE,"E25.1")])],"isStart":true});
            var Q90;
            Q90=makeQuery(id+"F1.opExtrude","CAP_EDGE",EDGE,{"disambiguationData":[OSD([sQuery(id+"F0.wireOp",EDGE,"E9.left")])],"isStart":true});
            var Q91;
            Q91=makeQuery(id+"F1.opExtrude","CAP_EDGE",EDGE,{"disambiguationData":[OSD([sQuery(id+"F0.wireOp",EDGE,"E1.right")])],"isStart":true});
            var Q92;
            {var subQ0=sQuery(id+"F0.wireOp",EDGE,"E1.bottom");Q92=makeQuery(id+"F1.opExtrude","CAP_EDGE",EDGE,{"disambiguationData":[OSD([subQ0]),TDD([makeQuery(id+"F0.imprint","IMPRINT",EDGE,{"disambiguationData":[TD([[makeQuery(id+"F0.imprint","INTERSECT",VERTEX,{"derivedFrom":[subQ0,sQuery(id+"F0.wireOp",EDGE,"E1.right")]}),1.0]])],"derivedFrom":subQ0})])],"isStart":true});}
            var Q93;
            Q93=makeQuery(id+"F1.opExtrude","CAP_EDGE",EDGE,{"disambiguationData":[OSD([sQuery(id+"F0.wireOp",EDGE,"E12.top")])],"isStart":true});
            var Q94;
            Q94=makeQuery(id+"F1.opExtrude","CAP_EDGE",EDGE,{"disambiguationData":[OSD([sQuery(id+"F0.wireOp",EDGE,"E12.bottom")])],"isStart":true});
            var Q95;
            Q95=makeQuery(id+"F1.opExtrude","CAP_EDGE",EDGE,{"disambiguationData":[OSD([sQuery(id+"F0.wireOp",EDGE,"E12.right")])],"isStart":true});
            var Q96;
            {var subQ0=sQuery(id+"F0.wireOp",EDGE,"E15");Q96=makeQuery(id+"F1.opExtrude","CAP_EDGE",EDGE,{"disambiguationData":[OSD([subQ0]),TDD([makeQuery(id+"F0.imprint","IMPRINT",EDGE,{"disambiguationData":[TD([[makeQuery(id+"F0.imprint","INTERSECT",VERTEX,{"disambiguationData":[OD(0.0)],"derivedFrom":[sQuery(id+"F0.wireOp",EDGE,"E8.right"),subQ0]}),1.0]])],"derivedFrom":subQ0})])],"isStart":true});}
            var Q97;
            {var subQ0=sQuery(id+"F0.wireOp",EDGE,"E15");Q97=makeQuery(id+"F1.opExtrude","CAP_EDGE",EDGE,{"disambiguationData":[OSD([subQ0]),TDD([makeQuery(id+"F0.imprint","IMPRINT",EDGE,{"disambiguationData":[TD([[makeQuery(id+"F0.imprint","INTERSECT",VERTEX,{"disambiguationData":[OD(1.0)],"derivedFrom":[sQuery(id+"F0.wireOp",EDGE,"E9.bottom"),subQ0]}),-1.0]])],"derivedFrom":subQ0})])],"isStart":true});}
            var Q98;
            {var subQ0=sQuery(id+"F0.wireOp",EDGE,"E9.bottom");Q98=makeQuery(id+"F1.opExtrude","CAP_EDGE",EDGE,{"disambiguationData":[OSD([subQ0]),TDD([makeQuery(id+"F0.imprint","IMPRINT",EDGE,{"disambiguationData":[TD([[makeQuery(id+"F0.imprint","INTERSECT",VERTEX,{"derivedFrom":[subQ0,sQuery(id+"F0.wireOp",EDGE,"E9.right")]}),1.0]])],"derivedFrom":subQ0})])],"isStart":true});}
            var Q99;
            Q99=makeQuery(id+"F1.opExtrude","CAP_EDGE",EDGE,{"disambiguationData":[OSD([sQuery(id+"F0.wireOp",EDGE,"E9.right")])],"isStart":true});
            var Q100;
            Q100=makeQuery(id+"F1.opExtrude","CAP_EDGE",EDGE,{"disambiguationData":[OSD([sQuery(id+"F0.wireOp",EDGE,"E9.top")])],"isStart":true});
            var Q101;
            {var subQ0=sQuery(id+"F0.wireOp",EDGE,"E15");Q101=makeQuery(id+"F1.opExtrude","CAP_EDGE",EDGE,{"disambiguationData":[OSD([subQ0]),TDD([makeQuery(id+"F0.imprint","IMPRINT",EDGE,{"disambiguationData":[TD([[makeQuery(id+"F0.imprint","INTERSECT",VERTEX,{"disambiguationData":[OD(0.0)],"derivedFrom":[sQuery(id+"F0.wireOp",EDGE,"E9.top"),subQ0]}),1.0]])],"derivedFrom":subQ0})])],"isStart":true});}
            var Q102;
            {var subQ0=sQuery(id+"F0.wireOp",EDGE,"E15");Q102=makeQuery(id+"F1.opExtrude","CAP_EDGE",EDGE,{"disambiguationData":[OSD([subQ0]),TDD([makeQuery(id+"F0.imprint","IMPRINT",EDGE,{"disambiguationData":[TD([[makeQuery(id+"F0.imprint","INTERSECT",VERTEX,{"disambiguationData":[OD(1.0)],"derivedFrom":[sQuery(id+"F0.wireOp",EDGE,"E8.right"),subQ0]}),-1.0]])],"derivedFrom":subQ0})])],"isStart":true});}
            var Q103;
            {var subQ0=sQuery(id+"F0.wireOp",EDGE,"E11.right");Q103=makeQuery(id+"F1.opExtrude","CAP_EDGE",EDGE,{"disambiguationData":[OSD([subQ0]),TDD([makeQuery(id+"F0.imprint","IMPRINT",EDGE,{"disambiguationData":[TD([[makeQuery(id+"F0.imprint","INTERSECT",VERTEX,{"derivedFrom":[sQuery(id+"F0.wireOp",EDGE,"E11.top"),subQ0]}),1.0]])],"derivedFrom":subQ0})])],"isStart":true});}
            var Q104;
            Q104=makeQuery(id+"F1.opExtrude","CAP_EDGE",EDGE,{"disambiguationData":[OSD([sQuery(id+"F0.wireOp",EDGE,"E11.top")])],"isStart":true});
            var Q105;
            {var subQ0=sQuery(id+"F0.wireOp",EDGE,"E11.left");Q105=makeQuery(id+"F1.opExtrude","CAP_EDGE",EDGE,{"disambiguationData":[OSD([subQ0]),TDD([makeQuery(id+"F0.imprint","IMPRINT",EDGE,{"disambiguationData":[TD([[makeQuery(id+"F0.imprint","INTERSECT",VERTEX,{"derivedFrom":[sQuery(id+"F0.wireOp",EDGE,"E11.top"),subQ0]}),1.0]])],"derivedFrom":subQ0})])],"isStart":true});}
            var Q106;
            {var subQ0=sQuery(id+"F0.wireOp",EDGE,"E8.right");Q106=makeQuery(id+"F1.opExtrude","CAP_EDGE",EDGE,{"disambiguationData":[OSD([subQ0]),TDD([makeQuery(id+"F0.imprint","IMPRINT",EDGE,{"disambiguationData":[TD([[makeQuery(id+"F0.imprint","INTERSECT",VERTEX,{"derivedFrom":[sQuery(id+"F0.wireOp",EDGE,"E8.top"),subQ0]}),1.0]])],"derivedFrom":subQ0})])],"isStart":true});}
            var Q107;
            Q107=makeQuery(id+"F1.opExtrude","CAP_EDGE",EDGE,{"disambiguationData":[OSD([sQuery(id+"F0.wireOp",EDGE,"E8.top")])],"isStart":true});
            var Q108;
            {var subQ0=sQuery(id+"F0.wireOp",EDGE,"E8.left");Q108=makeQuery(id+"F1.opExtrude","CAP_EDGE",EDGE,{"disambiguationData":[OSD([subQ0]),TDD([makeQuery(id+"F0.imprint","IMPRINT",EDGE,{"disambiguationData":[TD([[makeQuery(id+"F0.imprint","INTERSECT",VERTEX,{"derivedFrom":[sQuery(id+"F0.wireOp",EDGE,"E8.top"),subQ0]}),1.0]])],"derivedFrom":subQ0})])],"isStart":true});}
            var Q109;
            Q109=makeQuery(id+"F1.opExtrude","CAP_EDGE",EDGE,{"disambiguationData":[OSD([sQuery(id+"F0.wireOp",EDGE,"E25.3")])],"isStart":true});
            var Q110;
            Q110=makeQuery(id+"F1.opExtrude","CAP_EDGE",EDGE,{"disambiguationData":[OSD([sQuery(id+"F0.wireOp",EDGE,"E20.right")])],"isStart":true});
            var Q111;
            {var subQ0=sQuery(id+"F0.wireOp",EDGE,"E20.top");Q111=makeQuery(id+"F1.opExtrude","CAP_EDGE",EDGE,{"disambiguationData":[OSD([subQ0]),TDD([makeQuery(id+"F0.imprint","IMPRINT",EDGE,{"disambiguationData":[TD([[makeQuery(id+"F0.imprint","INTERSECT",VERTEX,{"derivedFrom":[subQ0,sQuery(id+"F0.wireOp",EDGE,"E20.right")]}),1.0]])],"derivedFrom":subQ0})])],"isStart":true});}
            var Q112;
            {var subQ0=sQuery(id+"F0.wireOp",EDGE,"E23");Q112=makeQuery(id+"F1.opExtrude","CAP_EDGE",EDGE,{"disambiguationData":[OSD([subQ0]),TDD([makeQuery(id+"F0.imprint","IMPRINT",EDGE,{"disambiguationData":[TD([[makeQuery(id+"F0.imprint","INTERSECT",VERTEX,{"disambiguationData":[OD(1.0)],"derivedFrom":[sQuery(id+"F0.wireOp",EDGE,"E17.bottom"),subQ0]}),-1.0]])],"derivedFrom":subQ0})])],"isStart":true});}
            var Q113;
            {var subQ0=sQuery(id+"F0.wireOp",EDGE,"E17.bottom");Q113=makeQuery(id+"F1.opExtrude","CAP_EDGE",EDGE,{"disambiguationData":[OSD([subQ0]),TDD([makeQuery(id+"F0.imprint","IMPRINT",EDGE,{"disambiguationData":[TD([[makeQuery(id+"F0.imprint","INTERSECT",VERTEX,{"derivedFrom":[subQ0,sQuery(id+"F0.wireOp",EDGE,"E17.right")]}),1.0]])],"derivedFrom":subQ0})])],"isStart":true});}
            var Q114;
            Q114=makeQuery(id+"F1.opExtrude","CAP_EDGE",EDGE,{"disambiguationData":[OSD([sQuery(id+"F0.wireOp",EDGE,"E17.right")])],"isStart":true});
            var Q115;
            {var subQ0=sQuery(id+"F0.wireOp",EDGE,"E17.top");Q115=makeQuery(id+"F1.opExtrude","CAP_EDGE",EDGE,{"disambiguationData":[OSD([subQ0]),TDD([makeQuery(id+"F0.imprint","IMPRINT",EDGE,{"disambiguationData":[TD([[makeQuery(id+"F0.imprint","INTERSECT",VERTEX,{"derivedFrom":[subQ0,sQuery(id+"F0.wireOp",EDGE,"E17.right")]}),1.0]])],"derivedFrom":subQ0})])],"isStart":true});}
            var Q116;
            {var subQ0=sQuery(id+"F0.wireOp",EDGE,"E23");Q116=makeQuery(id+"F1.opExtrude","CAP_EDGE",EDGE,{"disambiguationData":[OSD([subQ0]),TDD([makeQuery(id+"F0.imprint","IMPRINT",EDGE,{"disambiguationData":[TD([[makeQuery(id+"F0.imprint","INTERSECT",VERTEX,{"disambiguationData":[OD(1.0)],"derivedFrom":[sQuery(id+"F0.wireOp",EDGE,"E17.top"),subQ0]}),1.0]])],"derivedFrom":subQ0})])],"isStart":true});}
            var Q117;
            Q117=makeQuery(id+"F1.opExtrude","CAP_EDGE",EDGE,{"disambiguationData":[OSD([sQuery(id+"F0.wireOp",EDGE,"E19.right")])],"isStart":true});
            var Q118;
            Q118=makeQuery(id+"F1.opExtrude","CAP_EDGE",EDGE,{"disambiguationData":[OSD([sQuery(id+"F0.wireOp",EDGE,"E19.top")])],"isStart":true});
            var Q119;
            {var subQ0=sQuery(id+"F0.wireOp",EDGE,"E19.left");Q119=makeQuery(id+"F1.opExtrude","CAP_EDGE",EDGE,{"disambiguationData":[OSD([subQ0]),TDD([makeQuery(id+"F0.imprint","IMPRINT",EDGE,{"disambiguationData":[TD([[makeQuery(id+"F0.imprint","INTERSECT",VERTEX,{"derivedFrom":[sQuery(id+"F0.wireOp",EDGE,"E19.top"),subQ0]}),1.0]])],"derivedFrom":subQ0})])],"isStart":true});}
            var Q120;
            {var subQ0=sQuery(id+"F0.wireOp",EDGE,"E23");Q120=makeQuery(id+"F1.opExtrude","CAP_EDGE",EDGE,{"disambiguationData":[OSD([subQ0]),TDD([makeQuery(id+"F0.imprint","IMPRINT",EDGE,{"disambiguationData":[TD([[makeQuery(id+"F0.imprint","INTERSECT",VERTEX,{"disambiguationData":[OD(0.0)],"derivedFrom":[sQuery(id+"F0.wireOp",EDGE,"E16.right"),subQ0]}),-1.0]])],"derivedFrom":subQ0})])],"isStart":true});}
            var Q121;
            Q121=makeQuery(id+"F1.opExtrude","CAP_EDGE",EDGE,{"disambiguationData":[OSD([sQuery(id+"F0.wireOp",EDGE,"E16.right")])],"isStart":true});
            var Q122;
            Q122=makeQuery(id+"F1.opExtrude","CAP_EDGE",EDGE,{"disambiguationData":[OSD([sQuery(id+"F0.wireOp",EDGE,"E16.top")])],"isStart":true});
            var Q123;
            Q123=makeQuery(id+"F1.opExtrude","CAP_EDGE",EDGE,{"disambiguationData":[OSD([sQuery(id+"F0.wireOp",EDGE,"E16.left")])],"isStart":true});
            var Q124;
            {var subQ0=sQuery(id+"F0.wireOp",EDGE,"E23");Q124=makeQuery(id+"F1.opExtrude","CAP_EDGE",EDGE,{"disambiguationData":[OSD([subQ0]),TDD([makeQuery(id+"F0.imprint","IMPRINT",EDGE,{"disambiguationData":[TD([[makeQuery(id+"F0.imprint","INTERSECT",VERTEX,{"disambiguationData":[OD(0.0)],"derivedFrom":[sQuery(id+"F0.wireOp",EDGE,"E16.left"),subQ0]}),1.0]])],"derivedFrom":subQ0})])],"isStart":true});}
            var Q125;
            {var subQ0=sQuery(id+"F0.wireOp",EDGE,"E20.top");Q125=makeQuery(id+"F1.opExtrude","CAP_EDGE",EDGE,{"disambiguationData":[OSD([subQ0]),TDD([makeQuery(id+"F0.imprint","IMPRINT",EDGE,{"disambiguationData":[TD([[makeQuery(id+"F0.imprint","INTERSECT",VERTEX,{"derivedFrom":[subQ0,sQuery(id+"F0.wireOp",EDGE,"E20.left")]}),-1.0]])],"derivedFrom":subQ0})])],"isStart":true});}
            var Q126;
            Q126=makeQuery(id+"F1.opExtrude","CAP_EDGE",EDGE,{"disambiguationData":[OSD([sQuery(id+"F0.wireOp",EDGE,"E20.left")])],"isStart":true});
            var Q127;
            Q127=makeQuery(id+"F1.opExtrude","CAP_EDGE",EDGE,{"disambiguationData":[OSD([sQuery(id+"F0.wireOp",EDGE,"E20.bottom")])],"isStart":true});
            var Q128;
            {var subQ0=sQuery(id+"F0.wireOp",EDGE,"E23");Q128=makeQuery(id+"F1.opExtrude","CAP_EDGE",EDGE,{"disambiguationData":[OSD([subQ0]),TDD([makeQuery(id+"F0.imprint","IMPRINT",EDGE,{"disambiguationData":[TD([[makeQuery(id+"F0.imprint","INTERSECT",VERTEX,{"disambiguationData":[OD(0.0)],"derivedFrom":[sQuery(id+"F0.wireOp",EDGE,"E17.top"),subQ0]}),-1.0]])],"derivedFrom":subQ0})])],"isStart":true});}
            var Q129;
            {var subQ0=sQuery(id+"F0.wireOp",EDGE,"E17.top");Q129=makeQuery(id+"F1.opExtrude","CAP_EDGE",EDGE,{"disambiguationData":[OSD([subQ0]),TDD([makeQuery(id+"F0.imprint","IMPRINT",EDGE,{"disambiguationData":[TD([[makeQuery(id+"F0.imprint","INTERSECT",VERTEX,{"derivedFrom":[subQ0,sQuery(id+"F0.wireOp",EDGE,"E17.left")]}),-1.0]])],"derivedFrom":subQ0})])],"isStart":true});}
            var Q130;
            {var subQ0=sQuery(id+"F0.wireOp",EDGE,"E17.bottom");Q130=makeQuery(id+"F1.opExtrude","CAP_EDGE",EDGE,{"disambiguationData":[OSD([subQ0]),TDD([makeQuery(id+"F0.imprint","IMPRINT",EDGE,{"disambiguationData":[TD([[makeQuery(id+"F0.imprint","INTERSECT",VERTEX,{"derivedFrom":[subQ0,sQuery(id+"F0.wireOp",EDGE,"E17.left")]}),-1.0]])],"derivedFrom":subQ0})])],"isStart":true});}
            var Q131;
            Q131=makeQuery(id+"F1.opExtrude","CAP_EDGE",EDGE,{"disambiguationData":[OSD([sQuery(id+"F0.wireOp",EDGE,"E17.left")])],"isStart":true});
            var Q132;
            {var subQ0=sQuery(id+"F0.wireOp",EDGE,"E23");Q132=makeQuery(id+"F1.opExtrude","CAP_EDGE",EDGE,{"disambiguationData":[OSD([subQ0]),TDD([makeQuery(id+"F0.imprint","IMPRINT",EDGE,{"disambiguationData":[TD([[makeQuery(id+"F0.imprint","INTERSECT",VERTEX,{"disambiguationData":[OD(0.0)],"derivedFrom":[sQuery(id+"F0.wireOp",EDGE,"E17.bottom"),subQ0]}),1.0]])],"derivedFrom":subQ0})])],"isStart":true});}
            var Q133;
            {var subQ0=sQuery(id+"F0.wireOp",EDGE,"E19.left");Q133=makeQuery(id+"F1.opExtrude","CAP_EDGE",EDGE,{"disambiguationData":[OSD([subQ0]),TDD([makeQuery(id+"F0.imprint","IMPRINT",EDGE,{"disambiguationData":[TD([[makeQuery(id+"F0.imprint","INTERSECT",VERTEX,{"derivedFrom":[sQuery(id+"F0.wireOp",EDGE,"E19.bottom"),subQ0]}),-1.0]])],"derivedFrom":subQ0})])],"isStart":true});}
            var Q134;
            Q134=makeQuery(id+"F1.opExtrude","CAP_EDGE",EDGE,{"disambiguationData":[OSD([sQuery(id+"F0.wireOp",EDGE,"E25.5")])],"isStart":true});
            var Q135;
            Q135=makeQuery(id+"F1.opExtrude","CAP_EDGE",EDGE,{"disambiguationData":[OSD([sQuery(id+"F0.wireOp",EDGE,"E19.bottom")])],"isStart":true});
            var Q136;
            {var subQ0=sQuery(id+"F0.wireOp",EDGE,"E0.right");Q136=makeQuery(id+"F1.opExtrude","CAP_EDGE",EDGE,{"disambiguationData":[OSD([subQ0]),TDD([makeQuery(id+"F0.imprint","IMPRINT",EDGE,{"disambiguationData":[TD([[makeQuery(id+"F0.imprint","INTERSECT",VERTEX,{"derivedFrom":[sQuery(id+"F0.wireOp",EDGE,"E0.top"),subQ0]}),1.0]])],"derivedFrom":subQ0})])],"isStart":true});}
            var Q137;
            Q137=makeQuery(id+"F1.opExtrude","CAP_EDGE",EDGE,{"disambiguationData":[OSD([sQuery(id+"F0.wireOp",EDGE,"E0.top")])],"isStart":true});
            var Q138;
            {var subQ0=sQuery(id+"F0.wireOp",EDGE,"E0.left");Q138=makeQuery(id+"F1.opExtrude","CAP_EDGE",EDGE,{"disambiguationData":[OSD([subQ0]),TDD([makeQuery(id+"F0.imprint","IMPRINT",EDGE,{"disambiguationData":[TD([[makeQuery(id+"F0.imprint","INTERSECT",VERTEX,{"derivedFrom":[sQuery(id+"F0.wireOp",EDGE,"E0.top"),subQ0]}),1.0]])],"derivedFrom":subQ0})])],"isStart":true});}
            var Q139;
            {var subQ0=sQuery(id+"F0.wireOp",EDGE,"E7");Q139=makeQuery(id+"F1.opExtrude","CAP_EDGE",EDGE,{"disambiguationData":[OSD([subQ0]),TDD([makeQuery(id+"F0.imprint","IMPRINT",EDGE,{"disambiguationData":[TD([[makeQuery(id+"F0.imprint","INTERSECT",VERTEX,{"disambiguationData":[OD(1.0)],"derivedFrom":[sQuery(id+"F0.wireOp",EDGE,"E0.left"),subQ0]}),1.0]])],"derivedFrom":subQ0})])],"isStart":true});}
            var Q140;
            {var subQ0=sQuery(id+"F0.wireOp",EDGE,"E4.top");Q140=makeQuery(id+"F1.opExtrude","CAP_EDGE",EDGE,{"disambiguationData":[OSD([subQ0]),TDD([makeQuery(id+"F0.imprint","IMPRINT",EDGE,{"disambiguationData":[TD([[makeQuery(id+"F0.imprint","INTERSECT",VERTEX,{"derivedFrom":[subQ0,sQuery(id+"F0.wireOp",EDGE,"E4.left")]}),-1.0]])],"derivedFrom":subQ0})])],"isStart":true});}
            var Q141;
            Q141=makeQuery(id+"F1.opExtrude","CAP_EDGE",EDGE,{"disambiguationData":[OSD([sQuery(id+"F0.wireOp",EDGE,"E4.left")])],"isStart":true});
            var Q142;
            {var subQ0=sQuery(id+"F0.wireOp",EDGE,"E4.bottom");Q142=makeQuery(id+"F1.opExtrude","CAP_EDGE",EDGE,{"disambiguationData":[OSD([subQ0]),TDD([makeQuery(id+"F0.imprint","IMPRINT",EDGE,{"disambiguationData":[TD([[makeQuery(id+"F0.imprint","INTERSECT",VERTEX,{"derivedFrom":[subQ0,sQuery(id+"F0.wireOp",EDGE,"E4.left")]}),-1.0]])],"derivedFrom":subQ0})])],"isStart":true});}
            var Q143;
            {var subQ0=sQuery(id+"F0.wireOp",EDGE,"E7");Q143=makeQuery(id+"F1.opExtrude","CAP_EDGE",EDGE,{"disambiguationData":[OSD([subQ0]),TDD([makeQuery(id+"F0.imprint","IMPRINT",EDGE,{"disambiguationData":[TD([[makeQuery(id+"F0.imprint","INTERSECT",VERTEX,{"disambiguationData":[OD(0.0)],"derivedFrom":[sQuery(id+"F0.wireOp",EDGE,"E1.top"),subQ0]}),-1.0]])],"derivedFrom":subQ0})])],"isStart":true});}
            var Q144;
            {var subQ0=sQuery(id+"F0.wireOp",EDGE,"E1.top");Q144=makeQuery(id+"F1.opExtrude","CAP_EDGE",EDGE,{"disambiguationData":[OSD([subQ0]),TDD([makeQuery(id+"F0.imprint","IMPRINT",EDGE,{"disambiguationData":[TD([[makeQuery(id+"F0.imprint","INTERSECT",VERTEX,{"derivedFrom":[subQ0,sQuery(id+"F0.wireOp",EDGE,"E1.left")]}),-1.0]])],"derivedFrom":subQ0})])],"isStart":true});}
            var Q145;
            {var subQ0=sQuery(id+"F0.wireOp",EDGE,"E1.bottom");Q145=makeQuery(id+"F1.opExtrude","CAP_EDGE",EDGE,{"disambiguationData":[OSD([subQ0]),TDD([makeQuery(id+"F0.imprint","IMPRINT",EDGE,{"disambiguationData":[TD([[makeQuery(id+"F0.imprint","INTERSECT",VERTEX,{"derivedFrom":[subQ0,sQuery(id+"F0.wireOp",EDGE,"E1.left")]}),-1.0]])],"derivedFrom":subQ0})])],"isStart":true});}
            var Q146;
            Q146=makeQuery(id+"F1.opExtrude","CAP_EDGE",EDGE,{"disambiguationData":[OSD([sQuery(id+"F0.wireOp",EDGE,"E1.left")])],"isStart":true});
            var Q147;
            {var subQ0=sQuery(id+"F0.wireOp",EDGE,"E7");Q147=makeQuery(id+"F1.opExtrude","CAP_EDGE",EDGE,{"disambiguationData":[OSD([subQ0]),TDD([makeQuery(id+"F0.imprint","IMPRINT",EDGE,{"disambiguationData":[TD([[makeQuery(id+"F0.imprint","INTERSECT",VERTEX,{"disambiguationData":[OD(1.0)],"derivedFrom":[sQuery(id+"F0.wireOp",EDGE,"E1.bottom"),subQ0]}),-1.0]])],"derivedFrom":subQ0})])],"isStart":true});}
            var Q148;
            {var subQ0=sQuery(id+"F0.wireOp",EDGE,"E7");Q148=makeQuery(id+"F1.opExtrude","CAP_EDGE",EDGE,{"disambiguationData":[OSD([subQ0]),TDD([makeQuery(id+"F0.imprint","IMPRINT",EDGE,{"disambiguationData":[TD([[makeQuery(id+"F0.imprint","INTERSECT",VERTEX,{"disambiguationData":[OD(0.0)],"derivedFrom":[sQuery(id+"F0.wireOp",EDGE,"E0.right"),subQ0]}),1.0]])],"derivedFrom":subQ0})])],"isStart":true});}
            var Q149;
            {var subQ0=sQuery(id+"F0.wireOp",EDGE,"E7");Q149=makeQuery(id+"F1.opExtrude","CAP_EDGE",EDGE,{"disambiguationData":[OSD([subQ0]),TDD([makeQuery(id+"F0.imprint","IMPRINT",EDGE,{"disambiguationData":[TD([[makeQuery(id+"F0.imprint","INTERSECT",VERTEX,{"disambiguationData":[OD(0.0)],"derivedFrom":[sQuery(id+"F0.wireOp",EDGE,"E0.left"),subQ0]}),-1.0]])],"derivedFrom":subQ0})])],"isStart":true});}
            var Q150;
            {var subQ0=sQuery(id+"F0.wireOp",EDGE,"E7");Q150=makeQuery(id+"F1.opExtrude","CAP_EDGE",EDGE,{"disambiguationData":[OSD([subQ0]),TDD([makeQuery(id+"F0.imprint","IMPRINT",EDGE,{"disambiguationData":[TD([[makeQuery(id+"F0.imprint","INTERSECT",VERTEX,{"disambiguationData":[OD(0.0)],"derivedFrom":[sQuery(id+"F0.wireOp",EDGE,"E1.bottom"),subQ0]}),1.0]])],"derivedFrom":subQ0})])],"isStart":true});}
            var Q151;
            {var subQ0=sQuery(id+"F0.wireOp",EDGE,"E4.top");Q151=makeQuery(id+"F1.opExtrude","CAP_EDGE",EDGE,{"disambiguationData":[OSD([subQ0]),TDD([makeQuery(id+"F0.imprint","IMPRINT",EDGE,{"disambiguationData":[TD([[makeQuery(id+"F0.imprint","INTERSECT",VERTEX,{"derivedFrom":[subQ0,sQuery(id+"F0.wireOp",EDGE,"E4.right")]}),1.0]])],"derivedFrom":subQ0})])],"isStart":true});}
            var Q152;
            Q152=makeQuery(id+"F1.opExtrude","CAP_EDGE",EDGE,{"disambiguationData":[OSD([sQuery(id+"F0.wireOp",EDGE,"E4.right")])],"isStart":true});
            var Q153;
            {var subQ0=sQuery(id+"F0.wireOp",EDGE,"E4.bottom");Q153=makeQuery(id+"F1.opExtrude","CAP_EDGE",EDGE,{"disambiguationData":[OSD([subQ0]),TDD([makeQuery(id+"F0.imprint","IMPRINT",EDGE,{"disambiguationData":[TD([[makeQuery(id+"F0.imprint","INTERSECT",VERTEX,{"derivedFrom":[subQ0,sQuery(id+"F0.wireOp",EDGE,"E4.right")]}),1.0]])],"derivedFrom":subQ0})])],"isStart":true});}
            var Q154;
            {var subQ0=sQuery(id+"F0.wireOp",EDGE,"E0.right");Q154=makeQuery(id+"F1.opExtrude","CAP_EDGE",EDGE,{"disambiguationData":[OSD([subQ0]),TDD([makeQuery(id+"F0.imprint","IMPRINT",EDGE,{"disambiguationData":[TD([[makeQuery(id+"F0.imprint","INTERSECT",VERTEX,{"derivedFrom":[sQuery(id+"F0.wireOp",EDGE,"E0.bottom"),subQ0]}),-1.0]])],"derivedFrom":subQ0})])],"isStart":true});}
            var Q155;
            Q155=makeQuery(id+"F1.opExtrude","CAP_EDGE",EDGE,{"disambiguationData":[OSD([sQuery(id+"F0.wireOp",EDGE,"E0.bottom")])],"isStart":true});
            var Q156;
            {var subQ0=sQuery(id+"F0.wireOp",EDGE,"E0.left");Q156=makeQuery(id+"F1.opExtrude","CAP_EDGE",EDGE,{"disambiguationData":[OSD([subQ0]),TDD([makeQuery(id+"F0.imprint","IMPRINT",EDGE,{"disambiguationData":[TD([[makeQuery(id+"F0.imprint","INTERSECT",VERTEX,{"derivedFrom":[sQuery(id+"F0.wireOp",EDGE,"E0.bottom"),subQ0]}),-1.0]])],"derivedFrom":subQ0})])],"isStart":true});}
            var Q157;
            Q157=makeQuery(id+"F1.opExtrude","CAP_EDGE",EDGE,{"disambiguationData":[OSD([sQuery(id+"F0.wireOp",EDGE,"E3.right")])],"isStart":true});
            var Q158;
            Q158=makeQuery(id+"F1.opExtrude","CAP_EDGE",EDGE,{"disambiguationData":[OSD([sQuery(id+"F0.wireOp",EDGE,"E3.bottom")])],"isStart":true});
            var Q159;
            Q159=makeQuery(id+"F1.opExtrude","CAP_EDGE",EDGE,{"disambiguationData":[OSD([sQuery(id+"F0.wireOp",EDGE,"E3.left")])],"isStart":true});
            var Q160;
            Q160=makeQuery(id+"F1.opExtrude","SWEPT_EDGE",EDGE,{"disambiguationData":[OSD([sQuery(id+"F0.wireOp",EDGE,"E11.top"),sQuery(id+"F0.wireOp",EDGE,"E11.right")])]});
            var Q161;
            Q161=makeQuery(id+"F1.opExtrude","SWEPT_EDGE",EDGE,{"disambiguationData":[OSD([sQuery(id+"F0.wireOp",EDGE,"E11.top"),sQuery(id+"F0.wireOp",EDGE,"E11.left")])]});
            var Q162;
            Q162=makeQuery(id+"F1.opExtrude","SWEPT_EDGE",EDGE,{"disambiguationData":[OSD([sQuery(id+"F0.wireOp",EDGE,"E9.top"),sQuery(id+"F0.wireOp",EDGE,"E9.right")])]});
            var Q163;
            Q163=makeQuery(id+"F1.opExtrude","SWEPT_EDGE",EDGE,{"disambiguationData":[OSD([sQuery(id+"F0.wireOp",EDGE,"E9.bottom"),sQuery(id+"F0.wireOp",EDGE,"E9.right")])]});
            var Q164;
            Q164=makeQuery(id+"F1.opExtrude","SWEPT_EDGE",EDGE,{"disambiguationData":[OSD([sQuery(id+"F0.wireOp",EDGE,"E12.top"),sQuery(id+"F0.wireOp",EDGE,"E12.right")])]});
            var Q165;
            Q165=makeQuery(id+"F1.opExtrude","SWEPT_EDGE",EDGE,{"disambiguationData":[OSD([sQuery(id+"F0.wireOp",EDGE,"E12.bottom"),sQuery(id+"F0.wireOp",EDGE,"E12.right")])]});
            var Q166;
            Q166=makeQuery(id+"F1.opExtrude","SWEPT_EDGE",EDGE,{"disambiguationData":[OSD([sQuery(id+"F0.wireOp",EDGE,"E8.bottom"),sQuery(id+"F0.wireOp",EDGE,"E8.right")])]});
            var Q167;
            Q167=makeQuery(id+"F1.opExtrude","SWEPT_EDGE",EDGE,{"disambiguationData":[OSD([sQuery(id+"F0.wireOp",EDGE,"E8.bottom"),sQuery(id+"F0.wireOp",EDGE,"E8.left")])]});
            var Q168;
            Q168=makeQuery(id+"F1.opExtrude","SWEPT_EDGE",EDGE,{"disambiguationData":[OSD([sQuery(id+"F0.wireOp",EDGE,"E11.bottom"),sQuery(id+"F0.wireOp",EDGE,"E11.left")])]});
            var Q169;
            Q169=makeQuery(id+"F1.opExtrude","SWEPT_EDGE",EDGE,{"disambiguationData":[OSD([sQuery(id+"F0.wireOp",EDGE,"E11.bottom"),sQuery(id+"F0.wireOp",EDGE,"E11.right")])]});
            var Q170;
            Q170=makeQuery(id+"F1.opExtrude","SWEPT_EDGE",EDGE,{"disambiguationData":[OSD([sQuery(id+"F0.wireOp",EDGE,"E1.bottom"),sQuery(id+"F0.wireOp",EDGE,"E1.right")])]});
            var Q171;
            Q171=makeQuery(id+"F1.opExtrude","SWEPT_EDGE",EDGE,{"disambiguationData":[OSD([sQuery(id+"F0.wireOp",EDGE,"E9.bottom"),sQuery(id+"F0.wireOp",EDGE,"E9.left")])]});
            var Q172;
            Q172=makeQuery(id+"F1.opExtrude","SWEPT_EDGE",EDGE,{"disambiguationData":[OSD([sQuery(id+"F0.wireOp",EDGE,"E4.top"),sQuery(id+"F0.wireOp",EDGE,"E4.right")])]});
            var Q173;
            Q173=makeQuery(id+"F1.opExtrude","SWEPT_EDGE",EDGE,{"disambiguationData":[OSD([sQuery(id+"F0.wireOp",EDGE,"E4.bottom"),sQuery(id+"F0.wireOp",EDGE,"E4.right")])]});
            var Q174;
            Q174=makeQuery(id+"F1.opExtrude","SWEPT_EDGE",EDGE,{"disambiguationData":[OSD([sQuery(id+"F0.wireOp",EDGE,"E0.bottom"),sQuery(id+"F0.wireOp",EDGE,"E0.right")])]});
            var Q175;
            Q175=makeQuery(id+"F1.opExtrude","SWEPT_EDGE",EDGE,{"disambiguationData":[OSD([sQuery(id+"F0.wireOp",EDGE,"E0.bottom"),sQuery(id+"F0.wireOp",EDGE,"E0.left")])]});
            var Q176;
            Q176=makeQuery(id+"F1.opExtrude","SWEPT_EDGE",EDGE,{"disambiguationData":[OSD([sQuery(id+"F0.wireOp",EDGE,"E3.bottom"),sQuery(id+"F0.wireOp",EDGE,"E3.right")])]});
            var Q177;
            Q177=makeQuery(id+"F1.opExtrude","SWEPT_EDGE",EDGE,{"disambiguationData":[OSD([sQuery(id+"F0.wireOp",EDGE,"E3.bottom"),sQuery(id+"F0.wireOp",EDGE,"E3.left")])]});
            var Q178;
            Q178=makeQuery(id+"F1.opExtrude","SWEPT_EDGE",EDGE,{"disambiguationData":[OSD([sQuery(id+"F0.wireOp",EDGE,"E1.top"),sQuery(id+"F0.wireOp",EDGE,"E1.left")])]});
            var Q179;
            Q179=makeQuery(id+"F1.opExtrude","SWEPT_EDGE",EDGE,{"disambiguationData":[OSD([sQuery(id+"F0.wireOp",EDGE,"E1.bottom"),sQuery(id+"F0.wireOp",EDGE,"E1.left")])]});
            var Q180;
            Q180=makeQuery(id+"F1.opExtrude","SWEPT_EDGE",EDGE,{"disambiguationData":[OSD([sQuery(id+"F0.wireOp",EDGE,"E4.bottom"),sQuery(id+"F0.wireOp",EDGE,"E4.left")])]});
            var Q181;
            Q181=makeQuery(id+"F1.opExtrude","SWEPT_EDGE",EDGE,{"disambiguationData":[OSD([sQuery(id+"F0.wireOp",EDGE,"E4.top"),sQuery(id+"F0.wireOp",EDGE,"E4.left")])]});
            var Q182;
            Q182=makeQuery(id+"F1.opExtrude","SWEPT_EDGE",EDGE,{"disambiguationData":[OSD([sQuery(id+"F0.wireOp",EDGE,"E0.top"),sQuery(id+"F0.wireOp",EDGE,"E0.left")])]});
            var Q183;
            Q183=makeQuery(id+"F1.opExtrude","SWEPT_EDGE",EDGE,{"disambiguationData":[OSD([sQuery(id+"F0.wireOp",EDGE,"E0.top"),sQuery(id+"F0.wireOp",EDGE,"E0.right")])]});
            var Q184;
            Q184=makeQuery(id+"F1.opExtrude","SWEPT_EDGE",EDGE,{"disambiguationData":[OSD([sQuery(id+"F0.wireOp",EDGE,"E19.bottom"),sQuery(id+"F0.wireOp",EDGE,"E19.left")])]});
            var Q185;
            Q185=makeQuery(id+"F1.opExtrude","SWEPT_EDGE",EDGE,{"disambiguationData":[OSD([sQuery(id+"F0.wireOp",EDGE,"E17.bottom"),sQuery(id+"F0.wireOp",EDGE,"E17.left")])]});
            var Q186;
            Q186=makeQuery(id+"F1.opExtrude","SWEPT_EDGE",EDGE,{"disambiguationData":[OSD([sQuery(id+"F0.wireOp",EDGE,"E17.top"),sQuery(id+"F0.wireOp",EDGE,"E17.left")])]});
            var Q187;
            Q187=makeQuery(id+"F1.opExtrude","SWEPT_EDGE",EDGE,{"disambiguationData":[OSD([sQuery(id+"F0.wireOp",EDGE,"E20.bottom"),sQuery(id+"F0.wireOp",EDGE,"E20.left")])]});
            var Q188;
            Q188=makeQuery(id+"F1.opExtrude","SWEPT_EDGE",EDGE,{"disambiguationData":[OSD([sQuery(id+"F0.wireOp",EDGE,"E20.top"),sQuery(id+"F0.wireOp",EDGE,"E20.left")])]});
            var Q189;
            Q189=makeQuery(id+"F1.opExtrude","SWEPT_EDGE",EDGE,{"disambiguationData":[OSD([sQuery(id+"F0.wireOp",EDGE,"E16.top"),sQuery(id+"F0.wireOp",EDGE,"E16.left")])]});
            var Q190;
            Q190=makeQuery(id+"F1.opExtrude","SWEPT_EDGE",EDGE,{"disambiguationData":[OSD([sQuery(id+"F0.wireOp",EDGE,"E16.top"),sQuery(id+"F0.wireOp",EDGE,"E16.right")])]});
            var Q191;
            Q191=makeQuery(id+"F1.opExtrude","SWEPT_EDGE",EDGE,{"disambiguationData":[OSD([sQuery(id+"F0.wireOp",EDGE,"E19.top"),sQuery(id+"F0.wireOp",EDGE,"E19.left")])]});
            var Q192;
            Q192=makeQuery(id+"F1.opExtrude","SWEPT_EDGE",EDGE,{"disambiguationData":[OSD([sQuery(id+"F0.wireOp",EDGE,"E19.top"),sQuery(id+"F0.wireOp",EDGE,"E19.right")])]});
            var Q193;
            Q193=makeQuery(id+"F1.opExtrude","SWEPT_EDGE",EDGE,{"disambiguationData":[OSD([sQuery(id+"F0.wireOp",EDGE,"E17.top"),sQuery(id+"F0.wireOp",EDGE,"E17.right")])]});
            var Q194;
            Q194=makeQuery(id+"F1.opExtrude","SWEPT_EDGE",EDGE,{"disambiguationData":[OSD([sQuery(id+"F0.wireOp",EDGE,"E20.top"),sQuery(id+"F0.wireOp",EDGE,"E20.right")])]});
            var Q195;
            Q195=makeQuery(id+"F1.opExtrude","SWEPT_EDGE",EDGE,{"disambiguationData":[OSD([sQuery(id+"F0.wireOp",EDGE,"E17.bottom"),sQuery(id+"F0.wireOp",EDGE,"E17.right")])]});
            var Q196;
            Q196=makeQuery(id+"F1.opExtrude","SWEPT_EDGE",EDGE,{"disambiguationData":[OSD([sQuery(id+"F0.wireOp",EDGE,"E8.top"),sQuery(id+"F0.wireOp",EDGE,"E8.right")])]});
            var Q197;
            Q197=makeQuery(id+"F1.opExtrude","SWEPT_EDGE",EDGE,{"disambiguationData":[OSD([sQuery(id+"F0.wireOp",EDGE,"E8.top"),sQuery(id+"F0.wireOp",EDGE,"E8.left")])]});
            fillet(context, id + "F2", {"entities" : qUnion([Q0, Q1, Q2, Q3, Q4, Q5, Q6, Q7, Q8, Q9, Q10, Q11, Q12, Q13, Q14, Q15, Q16, Q17, Q18, Q19, Q20, Q21, Q22, Q23, Q24, Q25, Q26, Q27, Q28, Q29, Q30, Q31, Q32, Q33, Q34, Q35, Q36, Q37, Q38, Q39, Q40, Q41, Q42, Q43, Q44, Q45, Q46, Q47, Q48, Q49, Q50, Q51, Q52, Q53, Q54, Q55, Q56, Q57, Q58, Q59, Q60, Q61, Q62, Q63, Q64, Q65, Q66, Q67, Q68, Q69, Q70, Q71, Q72, Q73, Q74, Q75, Q76, Q77, Q78, Q79, Q80, Q81, Q82, Q83, Q84, Q85, Q86, Q87, Q88, Q89, Q90, Q91, Q92, Q93, Q94, Q95, Q96, Q97, Q98, Q99, Q100, Q101, Q102, Q103, Q104, Q105, Q106, Q107, Q108, Q109, Q110, Q111, Q112, Q113, Q114, Q115, Q116, Q117, Q118, Q119, Q120, Q121, Q122, Q123, Q124, Q125, Q126, Q127, Q128, Q129, Q130, Q131, Q132, Q133, Q134, Q135, Q136, Q137, Q138, Q139, Q140, Q141, Q142, Q143, Q144, Q145, Q146, Q147, Q148, Q149, Q150, Q151, Q152, Q153, Q154, Q155, Q156, Q157, Q158, Q159, Q160, Q161, Q162, Q163, Q164, Q165, Q166, Q167, Q168, Q169, Q170, Q171, Q172, Q173, Q174, Q175, Q176, Q177, Q178, Q179, Q180, Q181, Q182, Q183, Q184, Q185, Q186, Q187, Q188, Q189, Q190, Q191, Q192, Q193, Q194, Q195, Q196, Q197]), "radius" : 1 * mm, "tangentPropagation" : true, "allowEdgeOverflow" : false});
        }
    });
